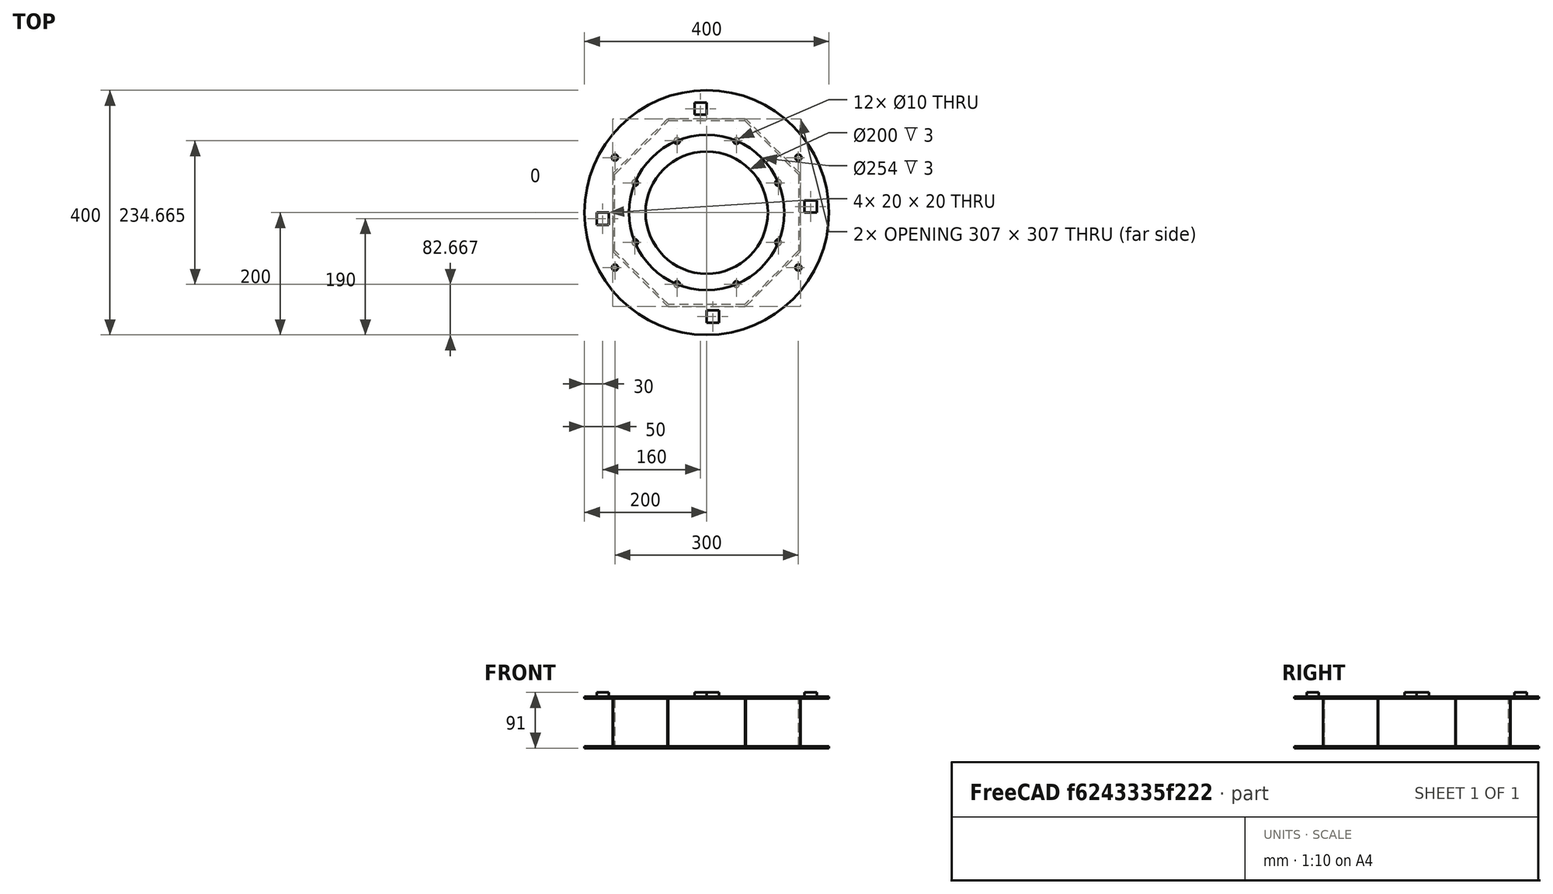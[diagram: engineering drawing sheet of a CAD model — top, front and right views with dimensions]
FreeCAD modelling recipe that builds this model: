
FCSTD DOCUMENT  (FreeCAD 0.21R33771 (Git))
Label: FEA_Model_MMv2
License: Creative Commons Attribution-ShareAlike 4.0
LicenseURL: https://creativecommons.org/licenses/by-sa/4.0/
objects: Fem::FemPostPipeline×13, Fem::FemMeshObjectPython×11, Fem::FemResultObjectPython×10, Sketcher::SketchObject×4, PartDesign::Pad×4, Fem::FemSolverObjectPython×4, Fem::ConstraintForce×4, PartDesign::Plane×1, PartDesign::PolarPattern×1, PartDesign::MultiTransform×1, App::MaterialObjectPython×1, PartDesign::Body×1, Fem::FemPostWarpVectorFilter×1, Fem::ConstraintFixed×1, App::TextDocument×1, Fem::FemAnalysis×1
note: 16 computed .brp shape members not serialized (recipe doc carries the construction recipe); baked Part::Feature solids carry a one-line shape summary decoded from their .brp

FEATURE [Sketcher::SketchObject] Sketch
  FullyConstrained = true
  MapMode = 5
  Support = -> [XY_Plane]
  sketch-geometry (22):
    g0: Circle CenterX=0 CenterY=0 CenterZ=0 NormalX=0 NormalY=0 NormalZ=1 AngleXU=0 Radius=100
    g1: Circle CenterX=0 CenterY=0 CenterZ=0 NormalX=0 NormalY=0 NormalZ=1 AngleXU=0 Radius=200
    g2: LineSegment StartX=-117.333 StartY=48.6008 StartZ=0 EndX=-117.333 EndY=-48.6008 EndZ=0
    g3: LineSegment StartX=-117.333 StartY=-48.6008 StartZ=0 EndX=-48.6008 EndY=-117.333 EndZ=0
    g4: LineSegment StartX=-48.6008 StartY=-117.333 StartZ=0 EndX=48.6008 EndY=-117.333 EndZ=0
    g5: LineSegment StartX=48.6008 StartY=-117.333 StartZ=0 EndX=117.333 EndY=-48.6008 EndZ=0
    g6: LineSegment StartX=117.333 StartY=-48.6008 StartZ=0 EndX=117.333 EndY=48.6008 EndZ=0
    g7: LineSegment StartX=117.333 StartY=48.6008 StartZ=0 EndX=48.6008 EndY=117.333 EndZ=0
    g8: LineSegment StartX=48.6008 StartY=117.333 StartZ=0 EndX=-48.6008 EndY=117.333 EndZ=0
    g9: LineSegment StartX=-48.6008 StartY=117.333 StartZ=0 EndX=-117.333 EndY=48.6008 EndZ=0
    g10: Circle CenterX=0 CenterY=0 CenterZ=0 NormalX=0 NormalY=0 NormalZ=1 AngleXU=0 Radius=127
    g11: Circle CenterX=-117.333 CenterY=48.6008 CenterZ=0 NormalX=0 NormalY=0 NormalZ=1 AngleXU=0 Radius=5
    g12: Circle CenterX=-48.6008 CenterY=117.333 CenterZ=0 NormalX=0 NormalY=0 NormalZ=1 AngleXU=0 Radius=5
    g13: Circle CenterX=48.6008 CenterY=117.333 CenterZ=0 NormalX=0 NormalY=0 NormalZ=1 AngleXU=0 Radius=5
    g14: Circle CenterX=117.333 CenterY=48.6008 CenterZ=0 NormalX=0 NormalY=0 NormalZ=1 AngleXU=0 Radius=5
    g15: Circle CenterX=117.333 CenterY=-48.6008 CenterZ=0 NormalX=0 NormalY=0 NormalZ=1 AngleXU=0 Radius=5
    g16: Circle CenterX=48.6008 CenterY=-117.333 CenterZ=0 NormalX=0 NormalY=0 NormalZ=1 AngleXU=0 Radius=5
    g17: Circle CenterX=-48.6008 CenterY=-117.333 CenterZ=0 NormalX=0 NormalY=0 NormalZ=1 AngleXU=0 Radius=5
    g18: Circle CenterX=-117.333 CenterY=-48.6008 CenterZ=0 NormalX=0 NormalY=0 NormalZ=1 AngleXU=0 Radius=5
    g19: LineSegment StartX=0 StartY=0 StartZ=0 EndX=-152 EndY=62.9605 EndZ=0
    g20: LineSegment StartX=0 StartY=0 StartZ=0 EndX=-152 EndY=-62.9605 EndZ=0
    g21: LineSegment StartX=-152 StartY=62.9605 StartZ=0 EndX=-152 EndY=-62.9605 EndZ=0
  constraints (49):
    c: Coincident(g0,g-1)
    c: Coincident(g1,g0)
    c: Diameter(g1) = 400
    c: Diameter(g0) = 200
    c: Coincident(g2,g3)
    c: Coincident(g3,g4)
    c: Coincident(g4,g5)
    c: Coincident(g5,g6)
    c: Coincident(g6,g7)
    c: Coincident(g7,g8)
    c: Coincident(g8,g9)
    c: Coincident(g9,g2)
    c: Equal(g2, g3-g9) x7
    c: PointOnObject(g2,g10)
    c: PointOnObject(g3,g10)
    c: PointOnObject(g4,g10)
    c: PointOnObject(g5,g10)
    c: PointOnObject(g6,g10)
    c: PointOnObject(g7,g10)
    c: PointOnObject(g8,g10)
    c: PointOnObject(g9,g10)
    c: Coincident(g10,g0)
    c: Vertical(g2)
    c: Diameter(g10) = 254
    c: Coincident(g11,g2)
    c: Diameter(g11) = 10
    c: Equal(g11,g12) = 10
    c: Coincident(g12,g8)
    c: Coincident(g13,g7)
    c: Equal(g13,g11)
    c: Coincident(g14,g6)
    c: Coincident(g15,g5)
    c: Coincident(g16,g4)
    c: Coincident(g17,g3)
    c: Coincident(g18,g2)
    c: Equal(g14,g15)
    c: Equal(g15,g16)
    c: Equal(g16,g17)
    c: Equal(g17,g18)
    c: Equal(g18,g11)
    c: Coincident(g19,g0)
    c: Coincident(g20,g0)
    c: PointOnObject(g18,g20)
    c: PointOnObject(g11,g19)
    c: Coincident(g21,g19)
    c: Coincident(g21,g20)
    c: Vertical(g21)
    c: DistanceX(g20,g0) = 152
    c: Distance(g21) = 125.921
FEATURE [PartDesign::Pad] Pad
  Direction = (0,0,1)
  Length = 3
  Length2 = 10
  Profile = -> Sketch
  ReferenceAxis = -> Sketch [N_Axis]
  Type = 0
FEATURE [Sketcher::SketchObject] Sketch001
  FullyConstrained = true
  MapMode = 5
  Support = -> [XY_Plane]
  sketch-geometry (7):
    g0: LineSegment StartX=-153.5 StartY=63 StartZ=0 EndX=-150.5 EndY=63 EndZ=0
    g1: LineSegment StartX=-150.5 StartY=63 StartZ=0 EndX=-150.5 EndY=-63 EndZ=0
    g2: LineSegment StartX=-150.5 StartY=-63 StartZ=0 EndX=-153.5 EndY=-63 EndZ=0
    g3: LineSegment StartX=-153.5 StartY=-63 StartZ=0 EndX=-153.5 EndY=63 EndZ=0
    g4: LineSegment StartX=-153.5 StartY=63 StartZ=0 EndX=-150.5 EndY=-63 EndZ=0
    g5: LineSegment StartX=-153.5 StartY=-63 StartZ=0 EndX=-150.5 EndY=63 EndZ=0
    g6: GeomPoint X=-152 Y=0 Z=0
  constraints (18):
    c: Coincident(g0,g1)
    c: Coincident(g1,g2)
    c: Coincident(g2,g3)
    c: Coincident(g3,g0)
    c: Horizontal(g0)
    c: Horizontal(g2)
    c: Vertical(g1)
    c: Vertical(g3)
    c: DistanceY(g3,g3) = 126
    c: DistanceX(g0,g0) = 3
    c: Coincident(g4,g0)
    c: Coincident(g4,g1)
    c: Coincident(g5,g2)
    c: Coincident(g5,g0)
    c: PointOnObject(g6,g4)
    c: PointOnObject(g6,g5)
    c: DistanceX(g6,g-1) = 152
    c: PointOnObject(g6,g-1)
FEATURE [PartDesign::Pad] Pad001
  BaseFeature = -> Pad
  Direction = (0,0,1)
  Length = 84
  Length2 = 10
  Profile = -> Sketch001
  ReferenceAxis = -> Sketch001 [N_Axis]
  Type = 0
FEATURE [PartDesign::Plane] DatumPlane
  AttachmentOffset = pos=(0,0,81) rot=(0,0,1;0rad)
  Length = 432
  MapMode = 5
  Placement = pos=(0,0,81) rot=(0,0,1;0rad)
  ResizeMode = 0
  Support = -> [XY_Plane]
  Width = 432
FEATURE [Sketcher::SketchObject] Sketch002
  FullyConstrained = true
  MapMode = 5
  Placement = pos=(0,0,81) rot=(0,0,1;0rad)
  Support = -> [DatumPlane]
  sketch-geometry (11):
    g0: Circle CenterX=0 CenterY=0 CenterZ=0 NormalX=0 NormalY=0 NormalZ=1 AngleXU=0 Radius=200
    g1: Circle CenterX=0 CenterY=0 CenterZ=0 NormalX=0 NormalY=0 NormalZ=1 AngleXU=0 Radius=127
    g2: Circle CenterX=-150 CenterY=90 CenterZ=0 NormalX=0 NormalY=0 NormalZ=1 AngleXU=0 Radius=5
    g3: Circle CenterX=-150 CenterY=-90 CenterZ=0 NormalX=0 NormalY=0 NormalZ=1 AngleXU=0 Radius=5
    g4: Circle CenterX=150 CenterY=90 CenterZ=0 NormalX=0 NormalY=0 NormalZ=1 AngleXU=0 Radius=5
    g5: Circle CenterX=150 CenterY=-90 CenterZ=0 NormalX=0 NormalY=0 NormalZ=1 AngleXU=0 Radius=5
    g6: LineSegment StartX=150 StartY=-90 StartZ=0 EndX=150 EndY=90 EndZ=0
    g7: LineSegment StartX=150 StartY=90 StartZ=0 EndX=-150 EndY=90 EndZ=0
    g8: LineSegment StartX=-150 StartY=90 StartZ=0 EndX=-150 EndY=-90 EndZ=0
    g9: LineSegment StartX=-150 StartY=-90 StartZ=0 EndX=150 EndY=-90 EndZ=0
    g10: GeomPoint X=0 Y=0 Z=0
  constraints (24):
    c: Diameter(g0) = 400
    c: Coincident(g1,g-1)
    c: Diameter(g1) = 254
    c: Coincident(g0,g1)
    c: Coincident(g6,g7)
    c: Coincident(g7,g8)
    c: Coincident(g8,g9)
    c: Coincident(g9,g6)
    c: Horizontal(g7)
    c: Horizontal(g9)
    c: Vertical(g6)
    c: Vertical(g8)
    c: Symmetric(g7,g6,g10)
    c: Coincident(g10,g0)
    c: Coincident(g7,g2)
    c: Coincident(g4,g6)
    c: Coincident(g5,g6)
    c: Coincident(g3,g8)
    c: Equal(g2,g4)
    c: Equal(g4,g5)
    c: Equal(g5,g3)
    c: Diameter(g2) = 10
    c: DistanceY(g8,g8) = 180
    c: DistanceX(g7,g7) = 300
FEATURE [PartDesign::Pad] Pad002
  BaseFeature = -> Pad001
  Direction = (0,0,1)
  Length = 3
  Length2 = 10
  Profile = -> Sketch002
  ReferenceAxis = -> Sketch002 [N_Axis]
  Type = 0
FEATURE [PartDesign::PolarPattern] PolarPattern
  Angle = 360
  Axis = -> Sketch001 [N_Axis]
  Occurrences = 8
FEATURE [PartDesign::MultiTransform] MultiTransform
  BaseFeature = -> Pad002
  Originals = -> [Pad001]
  Transformations = -> [PolarPattern]
FEATURE [App::MaterialObjectPython] MaterialSolid  # material (typed FeaturePython)
  Category = 0
  Material = AuthorAndLicense=(c) 2013 Juergen Riegel (CC-BY 3.0),CardName=Steel-Generic,Density=7900 kg/m^3,+9 more (map truncated)
FEATURE [Sketcher::SketchObject] Sketch003
  FullyConstrained = true
  MapMode = 5
  Placement = pos=(0,0,81) rot=(0,0,1;0rad)
  Support = -> [DatumPlane]
  sketch-geometry (20):
    g0: LineSegment StartX=160 StartY=20 StartZ=0 EndX=160 EndY=0 EndZ=0
    g1: LineSegment StartX=160 StartY=0 StartZ=0 EndX=180 EndY=0 EndZ=0
    g2: LineSegment StartX=180 StartY=0 StartZ=0 EndX=180 EndY=20 EndZ=0
    g3: LineSegment StartX=180 StartY=20 StartZ=0 EndX=160 EndY=20 EndZ=0
    g4: GeomPoint X=170 Y=10 Z=0
    g5: LineSegment StartX=-20 StartY=180 StartZ=0 EndX=-20 EndY=160 EndZ=0
    g6: LineSegment StartX=-20 StartY=160 StartZ=0 EndX=0 EndY=160 EndZ=0
    g7: LineSegment StartX=0 StartY=160 StartZ=0 EndX=0 EndY=180 EndZ=0
    g8: LineSegment StartX=0 StartY=180 StartZ=0 EndX=-20 EndY=180 EndZ=0
    g9: GeomPoint X=-10 Y=170 Z=0
    g10: LineSegment StartX=-180 StartY=0 StartZ=0 EndX=-180 EndY=-20 EndZ=0
    g11: LineSegment StartX=-180 StartY=-20 StartZ=0 EndX=-160 EndY=-20 EndZ=0
    g12: LineSegment StartX=-160 StartY=-20 StartZ=0 EndX=-160 EndY=0 EndZ=0
    g13: LineSegment StartX=-160 StartY=0 StartZ=0 EndX=-180 EndY=0 EndZ=0
    g14: GeomPoint X=-170 Y=-10 Z=0
    g15: LineSegment StartX=0 StartY=-160 StartZ=0 EndX=0 EndY=-180 EndZ=0
    g16: LineSegment StartX=0 StartY=-180 StartZ=0 EndX=20 EndY=-180 EndZ=0
    g17: LineSegment StartX=20 StartY=-180 StartZ=0 EndX=20 EndY=-160 EndZ=0
    g18: LineSegment StartX=20 StartY=-160 StartZ=0 EndX=0 EndY=-160 EndZ=0
    g19: GeomPoint X=10 Y=-170 Z=0
  constraints (52):
    c: Coincident(g0,g1)
    c: Coincident(g1,g2)
    c: Coincident(g2,g3)
    c: Coincident(g3,g0)
    c: Horizontal(g1)
    c: Horizontal(g3)
    c: Vertical(g0)
    c: Vertical(g2)
    c: Symmetric(g1,g0,g4)
    c: Coincident(g5,g6)
    c: Coincident(g6,g7)
    c: Coincident(g7,g8)
    c: Coincident(g8,g5)
    c: Horizontal(g6)
    c: Horizontal(g8)
    c: Vertical(g5)
    c: Vertical(g7)
    c: Symmetric(g6,g5,g9)
    c: Coincident(g10,g11)
    c: Coincident(g11,g12)
    c: Coincident(g12,g13)
    c: Coincident(g13,g10)
    c: Horizontal(g11)
    c: Horizontal(g13)
    c: Vertical(g10)
    c: Vertical(g12)
    c: Symmetric(g11,g10,g14)
    c: Coincident(g15,g16)
    c: Coincident(g16,g17)
    c: Coincident(g17,g18)
    c: Coincident(g18,g15)
    c: Horizontal(g16)
    c: Horizontal(g18)
    c: Vertical(g15)
    c: Vertical(g17)
    c: Symmetric(g16,g15,g19)
    c: DistanceX(g16,g16) = 20
    c: PointOnObject(g15,g-2)
    c: Equal(g17,g18)
    c: DistanceY(g19,g-1) = 170
    c: DistanceY(g-1,g9) = 170
    c: DistanceX(g-1,g4) = 170
    c: DistanceX(g14,g-1) = 170
    c: Equal(g18,g13)
    c: Equal(g13,g12)
    c: Equal(g12,g6)
    c: Equal(g6,g7)
    c: Equal(g7,g3)
    c: Equal(g3,g2)
    c: PointOnObject(g12,g-1)
    c: PointOnObject(g0,g-1)
    c: PointOnObject(g6,g-2)
FEATURE [PartDesign::Pad] Pad003
  BaseFeature = -> MultiTransform
  Direction = (0,0,1)
  Length = 10
  Length2 = 10
  Profile = -> Sketch003
  ReferenceAxis = -> Sketch003 [N_Axis]
  Type = 0
FEATURE [PartDesign::Body] Body
  Group = -> [Sketch,Pad,Sketch001,Pad001,DatumPlane,Sketch002,Pad002,MultiTransform,PolarPattern,Sketch003,Pad003]
  Origin = -> Origin
  Tip = -> Pad003
FEATURE [Fem::FemMeshObjectPython] FEMMeshGmsh  # FEM object (typed FeaturePython)
  Algorithm2D = 0
  Algorithm3D = 0
  CharacteristicLengthMax = 0
  CharacteristicLengthMin = 0
  CoherenceMesh = true
  ElementDimension = 0
  ElementOrder = 1
  GeometryTolerance = 1e-06
  GroupsOfNodes = false
  HighOrderOptimize = 0
  MeshSizeFromCurvature = 12
  OptimizeNetgen = false
  OptimizeStd = true
  Part = -> Pad003
  RecombinationAlgorithm = 0
  Recombine3DAll = false
  RecombineAll = false
  SecondOrderLinear = false
FEATURE [Fem::FemSolverObjectPython] SolverCalculix  # FEM object (typed FeaturePython)
  AnalysisType = 0
  BeamShellResultOutput3D = false
  BucklingFactors = 1
  EigenmodeHighLimit = 1000000
  EigenmodeLowLimit = 0
  EigenmodesCount = 10
  GeometricalNonlinearity = 0
  IterationsControlParameterCutb = 0.25,0.5,0.75,0.85,,,1.5,
  IterationsControlParameterIter = 4,8,9,200,10,400,,200,,
  IterationsControlParameterTimeUse = false
  IterationsThermoMechMaximum = 200
  IterationsUserDefinedIncrementations = false
  IterationsUserDefinedTimeStepLength = false
  MaterialNonlinearity = 0
  MatrixSolverType = 0
  SplitInputWriter = false
  ThermoMechSteadyState = true
  TimeEnd = 1
  TimeInitialStep = 1
FEATURE [Fem::FemPostWarpVectorFilter] WarpVector
  Factor = 49.51
  Vector = 0
FEATURE [Fem::FemPostPipeline] Pipeline_CalculiX_static_Results
  Filter = -> [WarpVector]
  Mode = 2
FEATURE [Fem::ConstraintFixed] ConstraintFixed
  NormalDirection = (1,-1e-16,0)
  Normals = (96) [(-1,0,0),(0.5,-0.866025,0),(0.5,0.866025,0),(-1,2.44929e-16,0),(-1,0,0),(0.5,-0.866025,0),(0.5,0.866025,0),(-1,2.44929e-16,0),(-1,0,0),+87 more]
  Points = (96) [(122.333,48.6008,3),(114.833,52.9309,3),(114.833,44.2707,3),(122.333,48.6008,3),(122.333,48.6008,1.5),(114.833,52.9309,1.5),(114.833,44.2707,1.5),+89 more]
  References = -> [Pad003]
  Scale = 2
FEATURE [Fem::FemSolverObjectPython] SolverCcxTools  # FEM object (typed FeaturePython)
  AnalysisType = 0
  BeamShellResultOutput3D = false
  BucklingFactors = 1
  EigenmodeHighLimit = 1000000
  EigenmodeLowLimit = 0
  EigenmodesCount = 10
  GeometricalNonlinearity = 0
  IterationsControlParameterCutb = 0.25,0.5,0.75,0.85,,,1.5,
  IterationsControlParameterIter = 4,8,9,200,10,400,,200,,
  IterationsControlParameterTimeUse = false
  IterationsThermoMechMaximum = 2000
  IterationsUserDefinedIncrementations = false
  IterationsUserDefinedTimeStepLength = false
  MaterialNonlinearity = 0
  MatrixSolverType = 0
  SplitInputWriter = false
  ThermoMechSteadyState = true
  TimeEnd = 1
  TimeInitialStep = 0.01
FEATURE [Fem::FemSolverObjectPython] SolverCalculix001  # FEM object (typed FeaturePython)
  AnalysisType = 0
  BeamShellResultOutput3D = false
  BucklingFactors = 1
  EigenmodeHighLimit = 1000000
  EigenmodeLowLimit = 0
  EigenmodesCount = 10
  GeometricalNonlinearity = 0
  IterationsControlParameterCutb = 0.25,0.5,0.75,0.85,,,1.5,
  IterationsControlParameterIter = 4,8,9,200,10,400,,200,,
  IterationsControlParameterTimeUse = false
  IterationsThermoMechMaximum = 2000
  IterationsUserDefinedIncrementations = false
  IterationsUserDefinedTimeStepLength = false
  MaterialNonlinearity = 0
  MatrixSolverType = 0
  SplitInputWriter = false
  ThermoMechSteadyState = true
  TimeEnd = 1
  TimeInitialStep = 0.01
FEATURE [Fem::FemPostPipeline] ResultPipeline
  Mode = 2
FEATURE [Fem::ConstraintForce] ConstraintForce
  Direction = -> Pad003 [Edge226]
  DirectionVector = (-0.707107,-0.707107,0)
  Force = 2850
  NormalDirection = (1,-1e-16,0)
  Points = (12) [(-145,90,84),(-152.5,94.3301,84),(-152.5,85.6699,84),(-145,90,84),(-145,90,82.5),(-152.5,94.3301,82.5),(-152.5,85.6699,82.5),(-145,90,82.5),+4 more]
  References = -> [Pad003]
  Reversed = true
  Scale = 2
FEATURE [Fem::ConstraintForce] ConstraintForce001
  Direction = -> Pad003 [Edge221]
  DirectionVector = (0.707107,-0.707107,0)
  Force = 2850
  NormalDirection = (1,-1e-16,0)
  Points = (12) [(-145,-90,84),(-152.5,-85.6699,84),(-152.5,-94.3301,84),(-145,-90,84),(-145,-90,82.5),(-152.5,-85.6699,82.5),(-152.5,-94.3301,82.5),(-145,-90,82.5),+4 more]
  References = -> [Pad003]
  Reversed = true
  Scale = 2
FEATURE [Fem::ConstraintForce] ConstraintForce002
  Direction = -> Pad003 [Edge233]
  DirectionVector = (0.707107,0.707107,0)
  Force = 2850
  NormalDirection = (1,-1e-16,0)
  Points = (12) [(155,-90,84),(147.5,-85.6699,84),(147.5,-94.3301,84),(155,-90,84),(155,-90,82.5),(147.5,-85.6699,82.5),(147.5,-94.3301,82.5),(155,-90,82.5),+4 more]
  References = -> [Pad003]
  Reversed = true
  Scale = 2
FEATURE [Fem::ConstraintForce] ConstraintForce003
  Direction = -> Pad003 [Edge238]
  DirectionVector = (-0.707107,0.707107,0)
  Force = 2850
  NormalDirection = (1,-1e-16,0)
  Points = (12) [(155,90,84),(147.5,94.3301,84),(147.5,85.6699,84),(155,90,84),(155,90,82.5),(147.5,94.3301,82.5),(147.5,85.6699,82.5),(155,90,82.5),(155,90,81),+3 more]
  References = -> [Pad003]
  Reversed = true
  Scale = 2
FEATURE [Fem::FemPostPipeline] Pipeline_CCX_Results
  Mode = 2
FEATURE [Fem::FemSolverObjectPython] SolverCcxTools001  # FEM object (typed FeaturePython)
  AnalysisType = 1
  BeamShellResultOutput3D = false
  BucklingFactors = 1
  EigenmodeHighLimit = 1000000
  EigenmodeLowLimit = 0
  EigenmodesCount = 10
  GeometricalNonlinearity = 0
  IterationsControlParameterCutb = 0.25,0.5,0.75,0.85,,,1.5,
  IterationsControlParameterIter = 4,8,9,200,10,400,,200,,
  IterationsControlParameterTimeUse = false
  IterationsThermoMechMaximum = 2000
  IterationsUserDefinedIncrementations = false
  IterationsUserDefinedTimeStepLength = false
  MaterialNonlinearity = 0
  MatrixSolverType = 0
  SplitInputWriter = false
  ThermoMechSteadyState = true
  TimeEnd = 1
  TimeInitialStep = 0.01
FEATURE [Fem::FemMeshObjectPython] CCX_EigenMode_1_Results_Mesh  # FEM object (typed FeaturePython)
FEATURE [Fem::FemResultObjectPython] CCX_EigenMode_1_Results  # FEM object (typed FeaturePython)
  DisplacementLengths = [36.1324,36.1311,13.4571,13.7361,13.6739,4.01533,3.89053,3.90667,7.97087,7.87766,8.06621,15.2902,15.0291,15.3227,13.6079,13.3328,13.549,3.83643,3.71415,3.72739,8.23995,8.13457,8.33602,15.4914,15.2266,15.5244,15.2129,15.5047,13.7167,13.4461,+7481 more]
  DisplacementVectors = (7511) [(0.814323,-0.0233713,36.1232),(-0.774746,0.108394,36.1226),(0.320202,0.191799,-13.4519),(0.332165,0.16695,-13.7311),(0.314468,0.210985,-13.6687),+7506 more]
  Eigenmode = 1
  EigenmodeFrequency = 549.841
  MaxShear = [326.363,690.179,4679.96,3288.88,2311.06,1362.16,1753.77,1194.57,1872.7,3116.93,2100.8,2626.94,5219.58,3126.36,2409.95,4439.1,2324.23,1156.75,1750.62,952.569,1577.39,3197.6,2128.25,3112.74,5216.01,3027.04,2280.24,2168.54,1534.44,1913.46,+7481 more]
  Mesh = -> CCX_EigenMode_1_Results_Mesh
  NodeNumbers = [1,2,3,4,5,6,7,8,9,10,11,12,13,14,15,16,17,18,19,20,21,22,23,24,25,26,27,28,29,30,31,32,33,34,35,36,37,38,39,40,41,42,43,44,45,46,47,48,49,50,51,52,53,54,55,56,57,58,59,60,61,62,63,64,65,66,67,68,69,+7442 more]
  NodeStrainXX = [0.0030878,-0.00487252,0.00209691,-0.0122655,-0.00823237,-0.0119638,-0.0136395,-0.0104847,0.0173261,0.0243868,0.0175075,0.00773248,-0.00128344,0.0106833,0.0090118,-0.00441965,0.0066169,0.0102703,0.0132308,0.00793071,-0.0137522,-0.0231871,+7489 more]
  NodeStrainXY = [-0.000585053,0.00067077,0.016592,0.00996236,0.00571926,-0.002227,-0.000847989,-0.00309526,-0.00129625,0.00251555,-0.000375481,0.00544919,0.0195384,0.00900183,-0.00725403,-0.0146643,-0.00575795,0.00227368,0.00162362,0.00241784,0.000148741,+7490 more]
  NodeStrainXZ = [0.000193783,-0.00042132,-0.0178555,-0.008414,-0.00605253,-0.00106414,-0.00188003,0.000762779,0.000496358,-0.00224992,-0.00350269,-0.00629089,-0.0182096,-0.00762218,-0.00599903,-0.0165288,-0.00563916,-0.00102333,-0.00189694,-0.000604541,+7491 more]
  NodeStrainYY = [-0.000980699,0.00396435,-0.0253691,-0.0207622,-0.0162432,0.000701833,0.00486517,0.000169847,0.00460781,-0.0055812,0.000871521,0.0198937,0.0298551,0.0215282,0.0161401,0.0262023,0.0181836,-0.00113573,-0.00512041,-0.00171642,-0.00183003,+7490 more]
  NodeStrainYZ = [-2.39986e-05,-8.19574e-05,-0.00925257,-0.00326347,-0.00607264,-0.00253608,-0.00523669,-0.00268604,0.00519186,0.0104622,0.00522376,0.00689375,0.00909602,0.00238753,-0.00287893,-0.00732202,-0.0040539,-0.00195279,-0.00507506,-0.00199882,+7491 more]
  NodeStrainZZ = [-0.000971946,0.000702889,0.00487403,0.0115162,0.00603745,0.0038036,0.00183234,0.00177993,-0.00449477,-0.0046059,-0.00610149,-0.00689876,-0.00542221,-0.010757,-0.00774489,-0.00425167,-0.0061495,-0.00292936,-0.00241025,-0.00147499,0.00392417,+7490 more]
  NodeStressXX = [606.024,-773.305,-1800.26,-4369.08,-3393.99,-2701.16,-2899.39,-2597.82,4677.77,5390.25,4110.11,3581.24,2473.63,4119.11,3394.94,1342.86,3170.02,2296.02,2693.22,1766.95,-3460.89,-5240.14,-4557.5,-4296.56,-1749.95,-4167.2,-802.523,1526.83,+7483 more]
  NodeStressXY = [-90.0082,103.195,2552.62,1532.67,879.886,-342.616,-130.46,-476.194,-199.424,387.007,-57.7663,838.337,3005.91,1384.9,-1116,-2256.04,-885.839,349.797,249.788,371.975,22.8832,-677.901,57.8014,-958.526,-2637.96,-1372.38,866.414,721.99,-786.365,+7482 more]
  NodeStressXZ = [29.8128,-64.8184,-2747,-1294.46,-931.159,-163.713,-289.236,117.351,76.3628,-346.141,-538.876,-967.83,-2801.48,-1172.64,-922.928,-2542.89,-867.564,-157.435,-291.836,-93.0063,-7.67475,-813.789,-519.898,-1167.99,-3015.96,-1144.45,-1613.09,+7484 more]
  NodeStressYY = [-19.8979,586.213,-6025.79,-5676.28,-4626.43,-752.602,-52.5145,-958.666,2721.11,779.782,1550.72,5452.21,7264.17,5787.55,4491.6,6053.93,4949.51,541.255,-130.045,282.778,-1626.71,-995.832,-2078.75,-6845.04,-6900.68,-5570.65,534.5,1292.9,+7483 more]
  NodeStressYZ = [-3.6921,-12.6088,-1423.47,-502.072,-934.252,-390.166,-805.645,-413.237,798.748,1609.57,803.655,1060.58,1399.39,367.312,-442.912,-1126.46,-623.676,-300.429,-780.779,-307.51,757.739,1797.89,652.862,844.166,1648.34,641.242,804.545,1503.35,+7483 more]
  NodeStressZZ = [-18.5513,84.4503,-1373.01,-710.362,-1198.64,-275.408,-519.104,-710.962,1320.71,929.829,477.954,1330.28,1836.9,820.588,816.982,1368.7,1205.96,265.311,286.902,319.922,-741.446,-1013.25,-687.845,-1637.66,-1468.97,-935.596,1564.57,1816.98,+7483 more]
  PrincipalMax = [620.123,594.602,2130.15,-127.089,-511.759,-56.4209,554.355,-336.99,4697.89,5433.85,4200.36,5878.95,8712.8,6582.51,5189.87,6962.19,5331.57,2384.61,2771.41,1872.23,-306.522,972.447,-377.945,-977.057,2395.74,-356.74,2448.38,3419.55,2470.16,+7482 more]
  PrincipalMed = [-19.9438,88.5119,-4099.43,-3923.79,-3573.43,-892.014,-1072.18,-1204.32,3069.2,2466.03,1939.66,3859.72,4588.27,3814.96,3143.69,3719.32,3310.8,646.866,808.497,530.322,-2061.23,-2798.91,-2311.71,-4599.67,-4479.07,-3905.89,960.276,2134.69,+7483 more]
  PrincipalMin = [-32.6042,-785.755,-7229.77,-6704.84,-5133.87,-2780.73,-2953.18,-2726.14,952.496,-800.017,-1.24336,625.06,-1726.36,329.782,369.965,-1916.02,683.118,71.1097,-729.828,-32.9056,-3461.3,-5422.75,-4634.44,-7202.54,-8036.27,-6410.82,-2112.1,+7484 more]
  ResultType = Fem::ResultMechanical
  Stats = [-9.62646,1.03652,-1.13205,2.49833,-38.9795,36.1232,0,38.9895,27.954,33045,-12778.5,50037.6,-18513,21074.7,-47505.4,14265,15.964,17997.5,0,0,0,0,0,0,0,0]
  Time = 0
  vonMises = [646.49,1209.52,8252.72,5719.09,4072.64,2417.37,3040.28,2094.78,3252.77,5400.75,3642.21,4590.41,9106.66,5426.89,4189.98,7781.25,4037.1,2086.09,3039.58,1695.21,2737.86,5568.05,3691.36,5415.48,9185.41,5268.92,4028.15,3858.57,2902.38,3381.27,+7481 more]
FEATURE [Fem::FemPostPipeline] Pipeline_CCX_EigenMode_1_Results
  Mode = 2
FEATURE [Fem::FemMeshObjectPython] CCX_EigenMode_2_Results_Mesh  # FEM object (typed FeaturePython)
FEATURE [Fem::FemResultObjectPython] CCX_EigenMode_2_Results  # FEM object (typed FeaturePython)
  DisplacementLengths = [6.51329,6.53195,7.57162,7.6697,7.76441,14.9444,14.6794,14.9693,13.2006,12.9296,13.1417,3.42169,3.30478,3.31378,8.67632,8.57171,8.77191,16.0953,15.8198,16.1245,14.3585,14.0734,14.3023,4.46825,4.337,4.35947,4.34683,4.36829,7.66528,7.57036,+7481 more]
  DisplacementVectors = (7511) [(-0.145361,0.0400156,-6.51154),(0.136509,0.499282,-6.51141),(-0.226865,-0.0161551,7.5682),(-0.224441,-0.00624625,7.66641),+7507 more]
  Eigenmode = 2
  EigenmodeFrequency = 553.372
  MaxShear = [227.809,319.677,2914.15,1795.08,1736.84,3291.25,5033,3340.74,3034.05,4553.4,2774.01,1131.31,1613.4,940.06,1503.66,3238.15,1941.03,2852.4,5939.57,3453.49,3073.78,5221.36,2924.27,1428.75,1928.39,1013.46,731.084,643.198,816.301,1109.01,+7481 more]
  Mesh = -> CCX_EigenMode_2_Results_Mesh
  NodeNumbers = <same value as first occurrence — deduplicated (x10 in doc)>
  NodeStrainXX = [-0.000534267,0.000894591,-0.0066109,0.000805463,-0.000318963,0.0262376,0.0326515,0.0274878,0.0229899,0.0306744,0.0197774,-0.00260738,-0.00557065,-0.00232457,-0.00127563,0.00778698,0.000144829,-0.0228726,-0.039422,-0.0242605,-0.0193644,+7490 more]
  NodeStrainXY = [-0.00143591,0.00190992,-0.00399284,-0.000417426,0.000431396,-0.00460572,-0.0146663,-0.00630401,0.00727778,0.0134133,0.00592587,-0.00212825,-0.000706947,-0.00250653,-0.000464858,0.00378831,-0.000372905,0.00465663,0.0173549,0.0099805,+7491 more]
  NodeStrainXZ = [-3.67507e-05,6.98318e-05,0.0096713,0.00491153,0.0033766,0.00691321,0.00945537,0.00102502,-0.000843828,-0.00533224,-0.00643939,-0.00158065,-0.0042878,-0.00174243,0.00413457,0.0109881,0.00391304,0.00494938,0.0116654,0.00532293,-0.00110557,+7490 more]
  NodeStrainYY = [0.000169063,-0.00073537,0.0213514,0.0157925,0.0160369,0.0109473,-0.00186988,0.0153707,0.015871,-0.000131314,0.00818204,0.0102649,0.0125375,0.00770444,-0.0133629,-0.0237003,-0.0182434,-0.0113823,0.000208486,-0.0112176,-0.0128824,+7490 more]
  NodeStrainYZ = [-8.03664e-05,-2.47868e-05,0.00420982,0.000511641,0.00316228,0.00726881,0.0183393,0.00874973,0.00762613,0.0159519,0.00726083,0.001324,0.00132411,-6.20299e-05,0.0016518,0.0043259,0.00207717,0.00704545,0.0191931,0.00889422,0.00947498,+7490 more]
  NodeStrainZZ = [0.000172538,-0.000125575,-0.00315999,-0.00460381,-0.00359594,-0.0108756,-0.00608187,-0.0101733,-0.00921824,-0.00807287,-0.00873185,-0.00182904,-0.00134988,-0.000965963,0.00349641,0.00337778,0.00432204,0.00911909,0.0105228,0.0101282,+7491 more]
  NodeStressXX = [-104.426,141.512,319.146,1507.86,1349.62,7072.26,7873.29,8000.27,6957.21,7311.86,5261.23,271.38,-208.909,151.67,-1481.88,-248.411,-1567.32,-6419.15,-9375.37,-6657.37,-5571.97,-7540.15,-6157.78,-687.418,123.113,-331.081,-333.684,180.815,+7483 more]
  NodeStressXY = [-220.909,293.833,-614.283,-64.2194,66.3687,-708.572,-2256.35,-969.847,1119.66,2063.59,911.673,-327.423,-108.761,-385.62,-71.5165,582.817,-57.37,716.405,2669.99,1535.46,-1366.22,-2514.84,-820.474,333.802,-31.3953,358.098,190.452,35.5568,+7483 more]
  NodeStressXZ = [-5.65396,10.7434,1487.89,755.62,519.478,1063.57,1454.67,157.696,-129.82,-820.345,-990.675,-243.176,-659.661,-268.067,636.088,1690.47,602.007,761.443,1794.68,818.912,-170.087,-1574.23,-962.765,-372.894,-857.109,-352.314,-351.678,-471.263,+7483 more]
  NodeStressYY = [3.77885,-109.252,4621.03,3813.56,3865.9,4719.91,2562.3,6136.11,5862,2572.52,3477.34,2251.73,2576.96,1694.59,-3341.46,-5092.61,-4396.29,-4651.4,-3278.38,-4650.77,-4574.73,-2950.38,-4510.54,-3060.34,-3057.21,-1941.77,311.273,619.451,-611.868,+7482 more]
  NodeStressYZ = [-12.3641,-3.81336,647.665,78.7139,486.505,1118.28,2821.42,1346.11,1173.25,2454.13,1117.05,203.693,203.708,-9.54306,254.123,665.522,319.565,1083.92,2952.78,1368.34,1457.69,3202.11,1073.47,144.132,363.545,129.235,443.21,346.394,562.622,+7482 more]
  NodeStressZZ = [4.31342,-15.4371,850.055,675.661,845.468,1362.54,1914.3,2206.26,2002.11,1350.74,875.203,391.125,440.439,360.687,-747.72,-926.75,-924.675,-1497.35,-1691.56,-1366.79,-1088.87,-1715.47,-1271.61,-601.439,-474.395,-461.099,464.218,661.868,+7483 more]
  PrincipalMax = [177.339,335.73,4763.15,3816.5,3950.8,7367.48,8730.94,8439.38,7705.67,8085.94,5701.48,2334.36,2607.26,1787.57,-368.871,1256.62,-547.93,-996.354,1443.86,-582.153,-477.459,1788.61,-699.394,-264.095,746.867,-16.9815,858.061,1116.74,173.769,+7482 more]
  PrincipalMed = [4.60477,-15.2836,2092.24,1954.25,1633.06,5002.27,4954,6145.35,5478.06,4170.05,3758.83,508.136,820.768,511.925,-1825.99,-2304.71,-1910.36,-4870.39,-5353.88,-4603.64,-4133.08,-5340.51,-4692.61,-963.507,-1045.45,-673.075,187.853,515.048,+7483 more]
  PrincipalMin = [-278.278,-303.624,-1065.16,226.336,477.126,784.968,-1335.05,1757.91,1637.58,-1020.87,153.468,71.7413,-619.541,-92.549,-3376.19,-5219.68,-4429.99,-6701.15,-10435.3,-7489.14,-6625.03,-8654.1,-6547.93,-3121.6,-3109.91,-2043.89,-604.107,+7484 more]
  ResultType = Fem::ResultMechanical
  Stats = [-1.3213,2.42548,-1.10315,9.64811,-37.3284,32.8618,0,37.3336,23.4424,32704.5,-14956.6,49674.6,-19728.2,21005.9,-46845.2,14052.6,12.8616,17811,0,0,0,0,0,0,0,0]
  Time = 0
  vonMises = [398.401,554.583,5053.32,3109.9,3063.87,5775.35,8807.43,5880.23,5316.64,7912.45,4876.11,2079.06,2799.85,1662.45,2604.83,5617.94,3411.39,5045.03,10323.4,6008.53,5355.65,9242.69,5176.55,2579.91,3342.84,1791.36,1267.74,1114.82,1416.04,1936.63,+7481 more]
FEATURE [Fem::FemPostPipeline] Pipeline_CCX_EigenMode_2_Results
  Mode = 2
FEATURE [Fem::FemMeshObjectPython] CCX_EigenMode_3_Results_Mesh  # FEM object (typed FeaturePython)
FEATURE [Fem::FemResultObjectPython] CCX_EigenMode_3_Results  # FEM object (typed FeaturePython)
  DisplacementLengths = [31.217,31.2143,11.9905,12.1456,12.1455,12.5627,12.3983,12.5618,12.7306,12.5681,12.7295,12.4572,12.2998,12.458,11.7886,11.6397,11.7797,11.1627,11.0257,11.1591,11.0755,10.9433,11.0805,11.5341,11.3969,11.5456,11.3825,11.5252,12.1205,11.9748,+7481 more]
  DisplacementVectors = (7511) [(-0.820739,0.0210017,-31.2062),(0.682129,-0.0663603,-31.2068),(0.298103,0.117281,-11.9862),(0.312323,0.0939068,-12.1412),(0.297959,0.147324,-12.141),+7506 more]
  Eigenmode = 3
  EigenmodeFrequency = 678.834
  MaxShear = [559.908,707.553,5032.04,3527.18,2764.19,3602.81,5128.34,3524.53,3538.45,5431.6,3549.66,2815.91,5073.6,3141,2538.38,4670.67,2710.45,2643.19,5073.6,2994.75,2836.84,4948.99,3074.48,3035.93,4710.93,2874.65,2107.29,2019.13,1666.83,2084.83,+7481 more]
  Mesh = -> CCX_EigenMode_3_Results_Mesh
  NodeNumbers = <same value as first occurrence — deduplicated (x10 in doc)>
  NodeStrainXX = [-0.00495147,0.00619949,0.00133501,-0.0146304,-0.00899124,-0.0294196,-0.0356375,-0.0299511,-0.0297828,-0.0402481,-0.0275088,-0.00902748,-0.00085625,-0.0134503,-0.0115766,0.00311605,-0.00790325,-0.0220898,-0.0355537,-0.0220697,-0.0201675,+7490 more]
  NodeStrainXY = [0.00045164,-0.000504169,0.0133483,0.00759626,0.00290537,0.00134883,0.0105882,0.00328865,-0.00343453,-0.00963628,-0.00241831,-0.00288177,-0.0159106,-0.00719426,0.00549341,0.0114458,0.0032998,0.00112725,0.0108922,0.00636012,-0.00501542,+7490 more]
  NodeStrainXZ = [-0.00031725,0.000483117,-0.020195,-0.00959158,-0.00706447,-0.00720964,-0.0103211,-0.00111607,0.000822391,0.00663366,0.00783074,0.00685272,0.0191741,0.00791875,0.00676081,0.0184487,0.00660248,0.00444091,0.0106174,0.00463932,-0.000990647,+7490 more]
  NodeStrainYY = [0.00225466,-0.00290552,-0.0316119,-0.024889,-0.0225362,-0.0136803,-0.00109254,-0.0187924,-0.0201497,-0.00122831,-0.010587,-0.0227485,-0.031513,-0.0221097,-0.0182311,-0.0306203,-0.0232201,-0.0112604,-0.00244684,-0.011805,-0.0133652,+7490 more]
  NodeStrainYZ = [1.949e-05,7.50706e-05,-0.00982677,-0.0027878,-0.00651686,-0.00789271,-0.0199874,-0.00980749,-0.0100541,-0.0202088,-0.00934921,-0.00699464,-0.00927176,-0.00218334,0.0031326,0.00807084,0.00426345,0.00641762,0.0175563,0.00816141,0.00932488,+7490 more]
  NodeStrainZZ = [0.00121211,-0.00176969,0.00694538,0.0132365,0.00786807,0.0128828,0.00817594,0.0119563,0.0120174,0.0113637,0.01229,0.00818662,0.0068162,0.0117887,0.00890927,0.00608543,0.00788699,0.00917822,0.0107147,0.00991046,0.0101578,0.00846089,+7489 more]
  NodeStressXX = [-933.077,1129.65,-2486.71,-5283.47,-4113.19,-8012.67,-8777.4,-8852.55,-8956.79,-9666.57,-7209.71,-4110.7,-3080.16,-4812.13,-4192.37,-1992.01,-3897.01,-6187.52,-8618.16,-6160.46,-5799.8,-8030.61,-6836.88,-4645.79,-2338.86,-4617.05,-653.572,+7484 more]
  NodeStressXY = [69.4831,-77.5644,2053.59,1168.65,446.98,207.512,1628.95,505.946,-528.389,-1482.51,-372.047,-443.349,-2447.78,-1106.81,845.141,1760.89,507.662,173.422,1675.73,978.48,-771.603,-1620,-205.792,-601.48,-2029.94,-1136.24,887.043,723.473,-849.367,+7482 more]
  NodeStressXZ = [-48.8077,74.3257,-3106.92,-1475.63,-1086.84,-1109.17,-1587.86,-171.702,126.522,1020.56,1204.73,1054.26,2949.86,1218.27,1040.12,2838.27,1015.77,683.216,1633.44,713.742,-152.407,-1560.68,-933.79,-1158.41,-2900.26,-1104.07,-1480.65,-1335.32,+7483 more]
  NodeStressYY = [175.559,-271.124,-7555.46,-6861.71,-6197.03,-5591.24,-3462.79,-7135.83,-7474.77,-3663.52,-4606.37,-6221.63,-7796.57,-6144.33,-5216.13,-7182.23,-6253.45,-4521.45,-3524.8,-4581.27,-4753.28,-3380.11,-4814.86,-6988.41,-6831.08,-5456.67,756.447,+7484 more]
  NodeStressYZ = [2.99846,11.5493,-1511.81,-428.892,-1002.59,-1214.26,-3074.98,-1508.84,-1546.79,-3109.05,-1438.34,-1076.1,-1426.43,-335.899,481.939,1241.67,655.915,987.326,2700.97,1255.6,1434.6,3219.59,1099.82,781.869,1540.9,598.313,806.899,1448.08,+7483 more]
  NodeStressZZ = [15.166,-96.3814,-1623.58,-996.249,-1519.45,-1504.6,-2036.87,-2405.25,-2525.99,-1726.28,-1086.83,-1462.38,-1899.78,-929.207,-1040.69,-1535.19,-1467.74,-1377.05,-1499.94,-1240.43,-1134.36,-1731.04,-1310.21,-1656.18,-1432.59,-975.251,1442.4,+7484 more]
  PrincipalMax = [179.897,1138.32,1750.37,-445.604,-897.921,-990.901,931.84,-1951.29,-2071.87,838.214,-342.699,-842.817,1305.21,-505.874,-617.619,1591.59,-980.257,-997.109,926.766,-640.997,-603.624,1299.9,-841.739,-1110.65,1774.29,-503.107,2289.95,3225.8,+7483 more]
  PrincipalMed = [17.6696,-99.3831,-5102.4,-5195.86,-4505.46,-5921.08,-5884.07,-7441.98,-7736.92,-5869.6,-5118.19,-4477.25,-5239.74,-4591.91,-4137.19,-4551.26,-4236.79,-4805.43,-5349.23,-4710.67,-4806.51,-5843.58,-5129.51,-4997.23,-4729.25,-4293.45,1179.96,+7484 more]
  PrincipalMin = [-939.918,-276.789,-8313.72,-7499.96,-6426.29,-8196.53,-9324.83,-9000.36,-9148.77,-10025,-7442.02,-6474.64,-8841.98,-6787.88,-5694.38,-7749.75,-6401.15,-6283.48,-9220.43,-6630.5,-6277.31,-8598.07,-6990.7,-7182.5,-7647.57,-6252.41,-1924.64,+7484 more]
  ResultType = Fem::ResultMechanical
  Stats = [-4.46728,4.09892,-3.60486,3.41194,-33.0743,2.02427,0,33.0859,48.3503,29255,-13037,39005.9,-18855.7,15657.7,-44318.7,12262.4,27.8907,15858.6,0,0,0,0,0,0,0,0]
  Time = 0
  vonMises = [1048.16,1335.27,8903.9,6230.48,4861.42,6379.87,9041.43,6413.48,6487.24,9493.98,6269.21,4945.51,8910.05,5521.85,4504.76,8222.7,4726.29,4724.07,8869.61,5297.27,5099.91,8848.35,5461.63,5326.74,8354.17,5062.54,3783.74,3645.37,3186.02,3748.81,+7481 more]
FEATURE [Fem::FemPostPipeline] Pipeline_CCX_EigenMode_3_Results
  Mode = 2
FEATURE [Fem::FemMeshObjectPython] CCX_EigenMode_4_Results_Mesh  # FEM object (typed FeaturePython)
FEATURE [Fem::FemResultObjectPython] CCX_EigenMode_4_Results  # FEM object (typed FeaturePython)
  DisplacementLengths = [39.9083,39.9016,8.00915,8.34118,8.26119,6.8274,6.64613,6.92752,9.24508,8.89757,9.17156,6.0076,5.84582,6.11394,8.65598,8.31787,8.58128,6.41875,6.24735,6.52273,8.9902,8.64699,8.91924,6.01444,5.85213,6.11894,5.83249,6.09414,8.31327,7.9904,+7481 more]
  DisplacementVectors = (7511) [(1.5938,0.0721658,39.8764),(-1.35173,-0.041129,39.8787),(-0.507994,0.0300343,7.99297),(-0.542016,0.0450534,8.32343),(-0.530265,0.0187294,8.24413),+7506 more]
  Eigenmode = 4
  EigenmodeFrequency = 935.02
  MaxShear = [1557.04,1763.69,3031.99,3392.41,2049.49,2247.1,3005.98,3550.91,4063.82,3560.99,2720.35,1754.36,2780.67,2914.55,2900.21,2817.68,2051.6,1963.99,3370.72,3306.15,3984.44,3921.15,2748.31,1934.89,2595.49,2880.06,1094.74,1652.73,1806.12,1283.46,+7481 more]
  Mesh = -> CCX_EigenMode_4_Results_Mesh
  NodeNumbers = <same value as first occurrence — deduplicated (x10 in doc)>
  NodeStrainXX = [0.0153367,-0.0164563,0.0150497,0.0265301,0.0171589,-0.00658496,-0.0118237,-0.0106641,-0.017178,-0.0237006,-0.0128704,0.0148474,0.0166423,0.0237075,0.0238551,0.0139364,0.0170309,-0.00317079,-0.0126432,-0.00706971,-0.0122119,-0.0199158,+7489 more]
  NodeStrainXY = [0.000768716,-0.000767976,-0.00604766,-0.00315324,-0.00118759,0.00304444,0.00703759,0.00362312,-0.000299972,-0.00352728,-0.000111535,0.00372447,0.00857555,0.00498989,-0.00270163,-0.00473565,-0.00162331,0.00391247,0.00976337,0.0072887,+7491 more]
  NodeStrainXZ = [0.00122953,-0.000815211,0.0134964,0.00714804,0.00509502,-0.00309883,-0.0049616,-0.00154585,0.00137241,0.00538704,0.00476275,-0.00381566,-0.00944415,-0.00428313,-0.00502451,-0.0123831,-0.00508676,0.00164844,0.0059293,0.00219045,-0.00115582,+7490 more]
  NodeStrainYY = [-0.00409494,0.0025398,0.0149907,0.0115834,0.00742426,-0.0198079,-0.0177296,-0.030099,-0.0340177,-0.0189825,-0.0209492,0.00184874,0.0079291,0.00565355,0.00916674,0.0168187,0.0104572,-0.0179291,-0.0198894,-0.0256657,-0.0316315,-0.0207241,+7489 more]
  NodeStrainYZ = [2.88667e-05,1.82835e-05,0.00695011,0.00201847,0.00459806,-0.00369552,-0.0117417,-0.00647512,-0.00871773,-0.0149853,-0.00665584,0.00377092,0.00513235,0.000875079,-0.00212478,-0.00615981,-0.00297484,0.00378892,0.0107791,0.00700318,0.00911591,+7490 more]
  NodeStrainZZ = [-0.00472385,0.00638212,-0.00830029,-0.0144511,-0.00590723,0.00709704,0.00827901,0.0134675,0.0157911,0.013492,0.0108093,-0.00334875,-0.00680129,-0.011848,-0.0118131,-0.0085621,-0.0068744,0.00499834,0.0100037,0.0120795,0.016371,0.011803,+7489 more]
  NodeStressXX = [3111.56,-3401.1,4823.81,6811.83,4794.74,-3239.51,-4273.76,-4790.11,-6727.93,-7014.45,-4635.11,3824.31,4610.75,5668.05,6117.17,4704.78,4998.65,-2345.68,-4544.58,-3471.03,-5048.65,-6391.32,-4756.56,4471.41,4174.45,5655.41,-138.719,-2112.31,+7483 more]
  NodeStressXY = [118.264,-118.15,-930.41,-485.114,-182.706,468.376,1082.71,557.403,-46.1495,-542.659,-17.1593,572.995,1319.31,767.675,-415.636,-728.561,-249.74,601.919,1502.06,1121.34,-464.287,-891.237,-11.4701,691.79,1084.4,849.265,-490.181,-865.371,+7483 more]
  NodeStressXZ = [189.158,-125.417,2076.36,1099.7,783.849,-476.742,-763.323,-237.823,211.14,828.776,732.731,-587.024,-1452.95,-658.944,-773.001,-1905.1,-782.578,253.606,912.199,336.992,-177.818,-1218.95,-589.999,575.148,1489.52,643.433,591.639,468.89,+7483 more]
  NodeStressYY = [122.075,-478.616,4814.75,4512.34,3297.11,-5273.8,-5182.36,-7780.1,-9318.66,-6288.6,-5877.99,1824.51,3270.26,2890.52,3857.43,5148.21,3987.3,-4616.18,-5659.39,-6331.95,-8036.27,-6515.67,-6429.08,2644.43,3019.95,2790.71,-413.454,-741.943,+7483 more]
  NodeStressYZ = [4.44103,2.81284,1069.25,310.534,707.394,-568.541,-1806.42,-996.172,-1341.19,-2305.44,-1023.98,580.141,789.592,134.628,-326.89,-947.663,-457.668,582.911,1658.32,1077.41,1402.45,2732.32,873.016,-388.933,-844.393,-261.411,-791.904,-1048.7,+7483 more]
  NodeStressZZ = [25.3197,112.509,1231.51,507.035,1246.11,-1134.59,-1181.03,-1077.55,-1655.76,-1292.52,-992.07,1024.89,1004.04,197.974,629.764,1243.48,1320.9,-1088.89,-1060.45,-524.992,-651.283,-1511.49,-1319.5,1130.73,871.322,310.996,-604.757,-428.345,+7483 more]
  PrincipalMax = [3127.77,117.063,5967.84,7069.86,4960.87,-931.873,-182.729,-906.725,-1419.02,-252.148,-655.166,4039.25,5593.49,5930.14,6280.15,5766.04,5179.03,-906.884,-106.048,-239.723,-379.515,30.6509,-1081.65,4754.61,5038.39,5942.75,865.997,773.761,+7483 more]
  PrincipalMed = [117.492,-473.952,4998.37,4476.31,3515.19,-3289.95,-4259.73,-4732.48,-6736.67,-6969.29,-4754.13,2103.94,3259.4,2725.38,3844.47,5199.76,4051.98,-2309,-4310.88,-3236.23,-5008.29,-6637.48,-4845.22,2607.11,3179.91,2631.72,-699.453,-1524.65,+7483 more]
  PrincipalMin = [13.6951,-3410.32,-96.1378,285.033,861.899,-5426.08,-6194.69,-8008.55,-9546.66,-7374.13,-6095.87,530.521,32.1537,101.03,479.742,130.669,1075.84,-4834.86,-6847.49,-6852.02,-8348.4,-7811.65,-6578.27,884.842,-152.582,182.644,-1323.47,-2531.71,+7483 more]
  ResultType = Fem::ResultMechanical
  Stats = [-19.5251,19.7549,-18.0926,18.161,-43.5429,41.0508,0,43.5622,62.6668,15473.6,-6760.51,21196.2,-9371.57,8298.72,-23192.7,6092.94,35.9156,8272.56,0,0,0,0,0,0,0,0]
  Time = 0
  vonMises = [3063.49,3272.15,5642.06,5929.89,3600.8,3893.68,5315.53,6156.5,7149.54,6928.44,4909.33,3044.03,4836.92,5056.49,5044.74,5374.65,3671.78,3447.82,5897.55,5734.78,6931.27,7326.13,4867.28,3358.06,4555.53,5006.99,1953.69,2934.53,3145.63,2321.17,+7481 more]
FEATURE [Fem::FemPostPipeline] Pipeline_CCX_EigenMode_4_Results
  Mode = 2
FEATURE [Fem::FemMeshObjectPython] CCX_EigenMode_5_Results_Mesh  # FEM object (typed FeaturePython)
FEATURE [Fem::FemResultObjectPython] CCX_EigenMode_5_Results  # FEM object (typed FeaturePython)
  DisplacementLengths = [7.17255,7.1547,6.57619,6.75447,6.8626,9.35218,8.9815,9.26607,6.339,6.17117,6.45148,8.99705,8.65047,8.92231,6.57106,6.40117,6.67899,9.35032,8.98415,9.26732,6.23773,6.05966,6.35066,8.79475,8.44929,8.7189,8.42791,8.69513,6.72978,6.55323,+7481 more]
  DisplacementVectors = (7511) [(0.289428,-0.575868,7.14353),(-0.253066,0.300023,7.14393),(0.212653,0.447285,-6.55751),(0.21381,0.456221,-6.73565),(0.220711,0.489206,-6.84158),+7506 more]
  Eigenmode = 5
  EigenmodeFrequency = 960.914
  MaxShear = [950.774,981.761,3186.87,2071.21,2786.76,4608.79,5032.48,4036.69,2968.95,4193.22,3551.76,3108.45,3590.87,2328.14,1722.94,3234.38,2797.69,3936,5222.4,3187.7,2149.41,3837.95,3520.86,3280.49,3563.94,2102.16,1358.63,1065.63,1075.53,1062.44,+7481 more]
  Mesh = -> CCX_EigenMode_5_Results_Mesh
  NodeNumbers = <same value as first occurrence — deduplicated (x10 in doc)>
  NodeStrainXX = [0.00286046,-0.00302115,0.00229233,-0.00171977,-0.00577422,-0.0300807,-0.0353798,-0.0279215,0.021299,0.0312992,0.0238523,0.0118773,0.00547162,0.0107052,-0.0014389,0.00260117,-0.00469806,-0.0261212,-0.0370686,-0.0227748,0.01603,0.0277541,+7489 more]
  NodeStrainXY = [-0.00589018,0.00611235,-0.00497504,-0.00667434,-0.00933299,-0.0132454,-0.00864712,-0.0118456,-0.012805,-0.0116712,-0.0125663,-0.00857154,-0.000969982,-0.00473182,-0.00712683,-0.00642017,-0.0101684,-0.0117629,-0.00751095,-0.00640119,+7491 more]
  NodeStrainXZ = [0.000230895,-0.000151738,-0.00978122,-0.00396006,-0.00373686,-0.00616349,-0.00909639,-0.000910268,-0.000449925,-0.00470259,-0.0055287,-0.00522334,-0.0134836,-0.00515925,0.00387044,0.00997694,0.0043846,0.00496503,0.0102971,0.0041021,+7491 more]
  NodeStrainYY = [-0.000815975,0.00053102,-0.0252496,-0.0174903,-0.0215984,-0.0209948,-0.0122376,-0.0207539,0.00754515,0.00282336,0.00862567,0.0223613,0.0278411,0.0175119,-0.0130158,-0.0247497,-0.0213468,-0.0174297,-0.0117248,-0.0148028,0.00209761,+7490 more]
  NodeStrainYZ = [-0.000304226,-0.000332043,-0.00371265,-5.8567e-05,-0.00301723,-0.00770158,-0.0177656,-0.00946649,0.00634754,0.0118696,0.00584699,0.00465305,0.00560013,0.00109346,0.00173028,0.00384074,0.00225637,0.00655456,0.0173778,0.00778505,-0.00371984,+7490 more]
  NodeStrainZZ = [-0.00086027,0.00116075,0.00646663,0.00461846,0.00885655,0.0170359,0.013803,0.0122747,-0.00592798,-0.0104144,-0.012223,-0.0107311,-0.00910904,-0.00863714,0.00281256,0.00648976,0.00840621,0.0141308,0.0157604,0.011387,-0.00402033,-0.00901141,+7489 more]
  NodeStressXX = [576.711,-618.181,-1550.1,-1948.23,-3024.81,-8555.45,-9344.71,-8495.71,5920.94,7550.82,6006.71,4539.68,3634.52,3906.16,-1564.7,-1406.6,-2758.01,-7413.28,-9514.37,-6525.82,4093.91,6777.12,6301.64,4527.41,2861.54,3412.64,298.437,-1308.7,+7483 more]
  NodeStressXY = [-906.181,940.362,-765.39,-1026.82,-1435.84,-2037.76,-1330.33,-1822.4,-1970,-1795.57,-1933.28,-1318.7,-149.228,-727.973,-1096.43,-987.719,-1564.37,-1809.68,-1155.53,-984.798,-1501.51,-1498.5,-1926.11,-1413.93,-445.006,-780.84,-488.475,+7484 more]
  NodeStressXZ = [35.5223,-23.3443,-1504.8,-609.24,-574.901,-948.229,-1399.44,-140.041,-69.2192,-723.475,-850.569,-803.59,-2074.39,-793.731,595.453,1534.91,674.554,763.851,1584.17,631.092,74.5737,1060.31,776.604,1031.3,2017.81,817.039,1111.37,835.194,+7483 more]
  NodeStressYY = [11.1058,-71.6939,-5787.32,-4374.47,-5459.3,-7157.62,-5784.37,-7393,3804.97,3169.92,3664.14,6152.6,7075.98,4953.35,-3345.76,-5614.42,-5319.35,-6076.12,-5615.33,-5299.36,1950.47,2966.79,4129.68,6629.85,6549.07,4380.19,-839.908,-1545.37,+7483 more]
  NodeStressYZ = [-46.8041,-51.0835,-571.177,-9.01031,-464.19,-1184.86,-2733.16,-1456.38,976.544,1826.09,899.537,715.854,861.558,168.225,266.198,590.883,347.134,1008.39,2673.51,1197.7,-572.283,-1792.92,-659.464,-530.543,-920.867,-379.099,-313.403,-499.063,+7483 more]
  NodeStressZZ = [4.29124,25.1878,-907.902,-973.12,-773.923,-1306.73,-1778.13,-2311.67,1732.18,1133.35,456.654,1061.46,1391.34,930.426,-910.625,-808.353,-741.968,-1220.66,-1386.84,-1270.16,1009.25,1120.89,690.207,1220.83,1113.03,1006.62,-941.157,-1128.44,+7483 more]
  PrincipalMax = [1245.75,639.222,309.917,-621.164,-632.202,-1032.68,-343.531,-1905.42,7158.55,8434.96,7301.02,7065.38,7272.82,5388.18,-504.566,461.536,-533.072,-992.265,1.0662,-918.411,4895.11,7700.57,7573.19,7483.67,6874.43,4954.48,1122.54,-370.246,+7483 more]
  PrincipalMed = [2.15492,20.3914,-2491.42,-1911.07,-2420.1,-5736.87,-6155.19,-6316.15,3078.89,3370.61,2628.98,3839.88,4737.95,3669.86,-1366.07,-2283.68,-2157.81,-4853.54,-6073.87,-4883.11,1562.22,3139.55,3016.85,3971.72,3902.65,3094.79,-1010.46,-1110.77,+7483 more]
  PrincipalMin = [-655.798,-1324.3,-6063.82,-4763.59,-6205.73,-10250.3,-10408.5,-9978.81,1220.65,48.52,197.506,848.476,91.0715,731.904,-3950.45,-6007.23,-6128.45,-8864.26,-10443.7,-7293.82,596.301,24.6738,531.481,922.695,-253.442,750.173,-1594.71,-2501.5,+7483 more]
  ResultType = Fem::ResultMechanical
  Stats = [-12.0264,11.9226,-11.8592,11.9006,-41.5505,42.2511,0,44.9947,49.6204,15645,-7236.26,23406.9,-9925.61,9586.18,-23906.4,6911.88,28.5032,8449.18,0,0,0,0,0,0,0,0]
  Time = 0
  vonMises = [1672.62,1738.76,5533.27,3671.54,4929.08,7983.23,8751.27,7001.75,5260.96,7314.93,6253,5385.27,6308.59,4078.3,3106.07,5623.43,4985.68,6817.76,9085.55,5575.67,3906.47,6686.73,6185.59,5686.68,6201.26,3649.11,2477.35,1874.13,1865.96,1912.39,+7481 more]
FEATURE [Fem::FemPostPipeline] Pipeline_CCX_EigenMode_5_Results
  Mode = 2
FEATURE [Fem::FemMeshObjectPython] CCX_EigenMode_6_Results_Mesh  # FEM object (typed FeaturePython)
FEATURE [Fem::FemResultObjectPython] CCX_EigenMode_6_Results  # FEM object (typed FeaturePython)
  DisplacementLengths = [6.68797,6.68627,3.14178,3.27845,3.2372,0.104079,0.107671,0.080179,0.31308,0.286811,0.305374,0.941799,0.907673,0.946854,0.304739,0.293045,0.294053,0.307025,0.270185,0.297393,2.27705,2.20982,2.33072,4.76755,4.59007,4.77916,4.58301,4.74287,+7483 more]
  DisplacementVectors = (7511) [(-0.313181,0.0537794,-6.68042),(0.264085,0.00693404,-6.68105),(0.210861,0.124236,-3.13223),(0.267713,0.108513,-3.2657),(0.245749,0.142884,-3.22469),+7506 more]
  Eigenmode = 6
  EigenmodeFrequency = 1142.52
  MaxShear = [360.398,372.342,5332.24,6133.87,3475.87,1694.17,1742.68,1358.45,338.413,272.981,302.927,551.998,730.112,743.265,590.944,523.382,357.879,289.374,561.414,561.027,3322.79,5926.41,5271.06,5666.55,6682.59,5971.7,2750.19,3531.11,3167.2,1815.5,+7481 more]
  Mesh = -> CCX_EigenMode_6_Results_Mesh
  NodeNumbers = <same value as first occurrence — deduplicated (x10 in doc)>
  NodeStrainXX = [-0.00340083,0.00346418,-0.0263841,-0.045636,-0.0269774,-0.0123216,-0.0108914,-0.00871271,-0.000671497,-0.000746364,-0.00155505,-0.0040505,-0.00396324,-0.00598689,-0.00493048,-0.0028174,-0.00284861,-0.000499323,-3.98838e-05,-0.000559212,+7491 more]
  NodeStrainXY = [0.000404048,-0.000382007,0.00813317,0.0104232,0.00259255,-0.00712035,-0.00684931,-0.00670123,0.000896797,0.00112041,0.00120072,0.000638489,-0.000446102,-0.000361967,0.00103251,0.000349692,0.000555959,0.00058623,0.00123317,0.00194956,+7491 more]
  NodeStrainXZ = [-0.000278012,0.000182101,-0.0255355,-0.0140228,-0.00979089,-0.00207106,-0.00332996,-0.000825721,3.27178e-05,0.000286777,0.000399647,0.0013898,0.00333431,0.00134779,0.000893143,0.00236525,0.000996262,7.20035e-05,0.00103847,0.000292071,+7491 more]
  NodeStrainYY = [0.00119608,-0.000508889,-0.0205066,-0.0174816,-0.01558,-0.000611415,0.00184726,0.00165915,0.00294651,0.00184542,0.00146375,-0.00292376,-0.00383381,-0.00253289,-0.000845675,-0.00186582,-0.00153759,-0.00226159,-0.00252453,-0.00373415,+7491 more]
  NodeStrainYZ = [2.49541e-05,2.32902e-05,-0.00955808,-0.0012232,-0.00465496,-0.00237261,-0.0046543,-0.00200282,3.16398e-05,-0.000145136,-0.000145695,-0.00104909,-0.00145875,-0.000265249,0.000515905,0.00136358,0.000670448,0.000975526,0.00279563,0.00159849,+7491 more]
  NodeStrainZZ = [0.000929269,-0.00132452,0.0150612,0.0255819,0.0126323,0.00506045,0.0029582,0.00132601,-0.00124043,-0.000449896,0.0001908,0.00194648,0.00234509,0.00324556,0.00218935,0.00144483,0.00101778,0.000751541,0.000741695,0.00166199,0.0104531,+7490 more]
  NodeStressXX = [-670.376,721.117,-7731.71,-11352,-7603.26,-2804,-2377.83,-2001.29,16.0675,-39.9218,-227.759,-1203.28,-1238.8,-1529.62,-1172.4,-807.105,-826.91,-308.67,-216.45,-389.652,-6125.79,-9267.87,-9481.58,-11245.6,-8875.27,-12080.8,243.122,6402.82,+7483 more]
  NodeStressXY = [62.1612,-58.7703,1251.26,1603.57,398.854,-1095.44,-1053.74,-1030.96,137.969,172.37,184.727,98.2291,-68.631,-55.6873,158.848,53.7987,85.5321,90.1892,189.718,299.932,1795.49,2393.1,2732.99,669.635,-489.359,-1268.58,-103.09,1231,-1520.28,+7482 more]
  NodeStressXZ = [-42.7711,28.0155,-3928.53,-2157.35,-1506.29,-318.625,-512.301,-127.034,5.0335,44.1195,61.4841,213.815,512.971,207.352,137.407,363.884,153.271,11.0775,159.765,44.934,-431.574,-1915.68,-1135.42,-2246.44,-5098.01,-2011.96,-2421.77,-2403.9,+7483 more]
  NodeStressYY = [36.8412,109.875,-6827.5,-7020.52,-5849.81,-1002.43,-418.031,-405.618,572.683,358.815,236.672,-1029.94,-1218.89,-998.239,-543.966,-660.709,-625.215,-579.788,-598.704,-878.104,-3941.93,-4648.62,-5883.79,-12399.5,-11285.2,-8837,-512.58,+7484 more]
  NodeStressYZ = [3.8391,3.58311,-1470.47,-188.185,-716.148,-365.017,-716.046,-308.126,4.86766,-22.3287,-22.4146,-161.398,-224.422,-40.8075,79.37,209.781,103.146,150.081,430.096,245.922,1021.24,3107.99,1177.29,1052.63,2076.82,715.305,1247.68,1106.34,+7483 more]
  NodeStressZZ = [-4.20678,-15.6064,-1355.52,-395.369,-1509.46,-129.838,-247.118,-456.869,-71.4604,5.68877,40.8342,-280.67,-268.288,-109.246,-77.0391,-151.377,-232.082,-116.229,-96.2071,-47.9295,-929.695,-1234.72,-951.785,-2356.32,-1723.18,-1298.85,-398.311,+7484 more]
  PrincipalMax = [42.2636,727.738,963.839,48.2048,-1028.44,6.02569,439.514,179.578,605.056,423.072,301.189,-210.342,-2.66212,-77.06,-40.1543,72.8271,-163.197,-66.1907,264.967,59.7589,-613.247,625.725,-650.34,-1749.48,1269.3,-826.363,2635.15,7677.81,7030.45,+7482 more]
  PrincipalMed = [-1.47232,104.595,-7177.92,-6596.56,-5953.92,-559.984,-436.654,-506.03,-15.9954,24.4013,53.2245,-989.21,-1260.43,-996.454,-531.209,-718.081,-642.055,-293.558,-318.468,-313.149,-3125.34,-4549.83,-4474.35,-11169.4,-11057.1,-8620.52,-437.686,+7484 more]
  PrincipalMin = [-678.533,-16.9466,-9700.65,-12219.5,-7980.18,-3382.31,-3045.84,-2537.32,-71.7704,-122.891,-304.666,-1314.34,-1462.89,-1563.59,-1222.04,-973.937,-878.955,-644.938,-857.86,-1062.3,-7258.83,-11227.1,-11192.5,-13082.6,-12095.9,-12769.8,+7485 more]
  ResultType = Fem::ResultMechanical
  Stats = [-20.3035,18.37,-5.70168,11.0182,-53.7494,106.014,0,106.146,17.8205,51067.9,-12622.7,43246.9,-49424.4,31078.5,-69996.1,6658.15,10.1014,29072.7,0,0,0,0,0,0,0,0]
  Time = 0
  vonMises = [699.954,691.966,9653.59,10636.5,6192.45,3143.78,3140.32,2447.22,650.734,489.238,527.556,982.637,1370.26,1299.37,1028.41,945.176,631.56,505.031,972.646,989.769,5812.06,10292.3,9243.72,10507.9,12877.2,10502.6,4774.38,6200.78,5565.29,3158.68,+7481 more]
FEATURE [Fem::FemPostPipeline] Pipeline_CCX_EigenMode_6_Results
  Mode = 2
FEATURE [Fem::FemMeshObjectPython] CCX_EigenMode_7_Results_Mesh  # FEM object (typed FeaturePython)
FEATURE [Fem::FemResultObjectPython] CCX_EigenMode_7_Results  # FEM object (typed FeaturePython)
  DisplacementLengths = [57.7184,57.7118,0.219055,0.25501,0.25093,0.754625,0.656536,0.731739,2.31489,2.24994,2.34962,4.56069,4.39276,4.57166,3.48026,3.33064,3.43374,0.633816,0.637,0.605936,0.0531877,0.0698163,0.0559054,0.568698,0.528117,0.54727,0.524135,0.545436,+7483 more]
  DisplacementVectors = (7511) [(-2.59166,-0.0980275,-57.6601),(2.30577,-0.191199,-57.6654),(-0.0150069,0.00100988,0.218538),(-0.0157122,0.0167211,0.253976),+7507 more]
  Eigenmode = 7
  EigenmodeFrequency = 1151.99
  MaxShear = [2554.07,3118.19,2146.84,1072.43,1129.26,1837.22,1913.36,1965,3272.33,4366.87,4160.6,5196.79,6524.35,6585.81,5534.63,5123.62,3735.5,1506.71,1811.67,1421.14,942.777,892.089,480.737,878.274,1480.26,775.639,554.991,758.368,743.568,527.69,+7481 more]
  Mesh = -> CCX_EigenMode_7_Results_Mesh
  NodeNumbers = <same value as first occurrence — deduplicated (x10 in doc)>
  NodeStrainXX = [-0.0237732,0.030652,-0.000992293,0.00130241,0.000233876,0.00983398,0.0136837,0.00942816,-0.0201308,-0.0302262,-0.0287749,-0.0294711,-0.0222441,-0.0470834,-0.039579,-0.0150225,-0.0243036,-0.00425324,0.00234019,0.00255759,0.00278694,+7490 more]
  NodeStrainXY = [0.000807531,-0.00148694,-0.0138541,-0.00678408,-0.00727036,0.00301233,0.00154708,0.00354165,0.00623066,0.00428967,0.00735569,0.00289887,-0.00616698,-0.0102411,0.0158095,0.0128832,0.00613846,-0.00826208,-0.0106589,-0.00856657,0.00533365,+7490 more]
  NodeStrainXZ = [-0.00411931,0.00251886,-0.000102807,0.000438264,-0.000517449,0.000745831,0.00179992,-0.0010457,0.00167052,0.00554848,0.00646614,0.0132401,0.03235,0.011325,0.00935525,0.0260856,0.0104395,-7.89389e-05,0.0018208,0.000991277,-0.00171703,+7490 more]
  NodeStrainYY = [0.00879817,-0.00932598,0.00227248,-0.00176723,0.0014983,0.0135033,0.00857342,0.0160757,-0.0236141,-0.0165006,-0.0166395,-0.0384739,-0.041584,-0.0297685,-0.0131878,-0.0219296,-0.0222801,0.00625615,0.00930442,0.00801713,0.00428732,0.00664694,+7489 more]
  NodeStrainYZ = [0.000369158,-2.72365e-05,-0.00033426,0.000179411,-0.000309186,0.00356976,0.00777431,0.00501229,-0.0084498,-0.0167033,-0.00813791,-0.00708886,-0.0132295,-0.00373968,0.00574868,0.0106937,0.00381189,-0.000188755,0.000599604,-0.00188405,+7491 more]
  NodeStrainZZ = [0.00660218,-0.00949993,0.000348454,0.000659683,-0.00233446,-0.00757384,-0.00639441,-0.00590541,0.010716,0.0153471,0.0178404,0.0224219,0.0205173,0.0308029,0.0211327,0.0114403,0.0149857,0.001283,-0.00347727,-0.00330725,-0.0017597,-0.00172631,+7489 more]
  NodeStressXX = [-4623.51,6080.25,35.2597,222.855,-33.5132,3331.77,3935.49,3711.85,-6908.07,-8270.9,-7608.51,-9786.68,-8419.58,-12557,-9739.15,-5254.83,-7384.93,-275.2,1302.41,1232.03,1041.98,615.689,743.887,86.6307,2280.27,764.032,-636.181,-1583.12,-282,+7482 more]
  NodeStressXY = [124.236,-228.761,-2131.41,-1043.7,-1118.52,463.436,238.013,544.869,958.563,659.949,1131.65,445.98,-948.766,-1575.56,2432.23,1982.04,944.378,-1271.09,-1639.83,-1317.93,820.561,649.13,437.052,544.357,496.378,631.276,-3.2689,-294.222,-129.377,+7482 more]
  NodeStressXZ = [-633.74,387.517,-15.8164,67.4252,-79.6075,114.743,276.91,-160.876,257.004,853.612,994.791,2036.93,4976.92,1742.3,1439.27,4013.17,1606.07,-12.1444,280.123,152.504,-264.159,-203.161,-96.3091,83.1816,749.697,34.3267,198.136,-359.381,50.1647,+7482 more]
  NodeStressYY = [387.466,-70.2136,537.533,-249.397,161.014,3896.28,3149.3,4734.55,-7443.97,-6159.27,-5741.53,-11171.7,-11395,-9893.12,-5678.97,-6317.45,-7073.62,1341.63,2373.83,2071.96,1272.81,1610.91,632.341,-341.457,181.84,-67.4416,-141.685,-477.91,+7483 more]
  NodeStressYZ = [56.7936,-4.19023,-51.4247,27.6016,-47.5671,549.194,1196.05,771.121,-1299.97,-2569.74,-1251.99,-1090.59,-2035.31,-575.336,884.412,1645.18,586.444,-29.0392,92.2467,-289.853,-364.65,-259.807,52.2387,-568.539,-379.349,-174.158,104.338,-127.605,+7483 more]
  NodeStressZZ = [49.6218,-96.9747,241.529,123.974,-428.641,653.649,846.554,1352.84,-2162.42,-1259.63,-436.925,-1803.14,-1840.91,-574.437,-398.887,-1183.62,-1340.42,576.53,407.42,329.746,342.496,322.718,305.181,518.975,450.872,363.087,380.307,-352.565,+7483 more]
  PrincipalMax = [396.865,6112.92,2432.91,1058.15,1186.71,4237.07,4157.15,5085.4,-1859.57,-124.73,-83.9473,-1221.11,1233.49,-259.963,107.921,2001.92,-836.796,2039.87,3565.81,3073.49,2100.52,1993.71,1130.46,850.56,2598.37,1107.95,435.578,-242.343,227.459,+7482 more]
  PrincipalMed = [127.99,-76.3962,242.179,125.975,-416.03,3082,3443.76,3558.44,-6250.66,-6706.59,-5297.88,-9925.73,-11073.8,-9333.01,-4963.6,-6512.49,-6654.37,576.658,575.389,329.043,341.806,346.083,381.957,319.575,676.76,395.054,-158.733,-412.172,-264.474,+7482 more]
  PrincipalMin = [-4711.28,-123.457,-1860.76,-1086.7,-1071.82,562.628,330.435,1155.4,-8404.23,-8858.48,-8405.14,-11614.7,-11815.2,-13431.6,-10961.3,-8245.33,-8307.8,-973.564,-57.5377,231.202,214.963,209.528,168.989,-905.987,-362.145,-443.328,-674.404,+7484 more]
  ResultType = Fem::ResultMechanical
  Stats = [-20.6072,20.0398,-9.72749,3.7352,-57.6654,111.459,0,111.547,75.7531,46458.3,-17753.8,54325.2,-52301.9,35433.6,-70569.2,11610.5,43.4223,26407.7,0,0,0,0,0,0,0,0]
  Time = 0
  vonMises = [4979.15,6212.98,3718.69,1862.78,2012.43,3254.46,3524.59,3431.56,5777.2,7881.3,7282.94,9660.47,12694.2,11675,9597.43,9500.1,6796.84,2610.07,3352,2794.65,1825.44,1719.97,874.658,1560.35,2601.59,1344.91,962.076,1439.36,1312.25,935.851,2135.08,+7480 more]
FEATURE [Fem::FemPostPipeline] Pipeline_CCX_EigenMode_7_Results
  Mode = 2
FEATURE [Fem::FemMeshObjectPython] CCX_EigenMode_8_Results_Mesh  # FEM object (typed FeaturePython)
FEATURE [Fem::FemResultObjectPython] CCX_EigenMode_8_Results  # FEM object (typed FeaturePython)
  DisplacementLengths = [6.53354,6.53043,2.1747,2.30202,2.3062,1.92926,1.82698,1.89867,0.0704753,0.0558524,0.0790583,0.465424,0.443856,0.472065,0.920632,0.873764,0.907305,1.53063,1.47481,1.55257,2.87873,2.70879,2.89795,0.379548,0.334348,0.32505,0.391477,0.392642,+7483 more]
  DisplacementVectors = (7511) [(-0.317315,-0.155073,-6.52399),(0.269132,-0.0846636,-6.52433),(0.196685,0.0123707,-2.16575),(0.234392,0.00348978,-2.29005),+7507 more]
  Eigenmode = 8
  EigenmodeFrequency = 1176.24
  MaxShear = [390.603,445.038,4095.64,4283.78,3138.32,3846.47,4101.93,3209.22,1676.15,2216.31,1910.05,1521.68,1654.03,998.086,610.18,603.326,645.383,1916.18,2930.25,2907.35,4808.86,7452.14,6280.92,4637.17,4444.08,4163.3,615.848,1921.33,2172.76,1510.45,+7481 more]
  Mesh = -> CCX_EigenMode_8_Results_Mesh
  NodeNumbers = <same value as first occurrence — deduplicated (x10 in doc)>
  NodeStrainXX = [-0.00357604,0.00412124,-0.0168676,-0.0310532,-0.0193844,-0.0251698,-0.0255673,-0.0207539,-0.0111014,-0.0149315,-0.0134229,-0.0024731,-0.00103327,-0.00508913,-0.005291,-0.0046777,-0.00390389,0.00790615,0.0123257,0.00831613,0.0287017,+7490 more]
  NodeStrainXY = [-0.000340519,6.38447e-05,0.00235354,0.0036849,-0.00240739,-0.0132288,-0.0116132,-0.0118798,0.005537,0.00599714,0.00532252,0.00316035,0.00216023,0.00175707,0.00172192,0.001964,0.00209107,0.000936267,-0.00135377,-0.00366902,-0.00955809,+7490 more]
  NodeStrainXZ = [-0.000495478,0.000189079,-0.0202568,-0.0104711,-0.00794806,-0.00477226,-0.00778913,-0.0020568,0.00172937,0.00418128,0.00348398,0.00276494,0.00614815,0.00206187,0.00019987,1.64678e-05,-1.46196e-05,-0.00159742,-0.0059281,-0.0020542,+7491 more]
  NodeStrainYY = [0.000326779,-0.000576205,-0.0253817,-0.0197403,-0.022342,-0.0137093,-0.00914578,-0.0132797,-0.00667633,-0.00309654,-0.00449162,-0.0125001,-0.0116954,-0.00700771,0.00119598,0.00193602,0.00327469,0.0159906,0.0178601,0.022468,0.0279299,+7490 more]
  NodeStrainYZ = [-5.3668e-05,8.95868e-07,-0.00775501,-0.00101701,-0.00411233,-0.00581613,-0.013349,-0.0066734,-0.00349248,-0.0067815,-0.00354385,-0.00266867,-0.00311544,-0.00133899,-0.000481877,-0.000559595,-0.000578722,-0.00421077,-0.0119932,-0.00692278,+7491 more]
  NodeStrainZZ = [0.00137346,-0.001651,0.0137601,0.0195807,0.0133827,0.0137816,0.0112224,0.00959651,0.00544088,0.00596681,0.00679144,0.00468649,0.00393974,0.00400143,0.00188203,0.000661229,-0.000160679,-0.00714784,-0.00995118,-0.011633,-0.0206582,-0.0220512,+7489 more]
  NodeStressXX = [-766.599,852.58,-5882.23,-8378.89,-6252.63,-6768.14,-6643.9,-6012.58,-3131.4,-3688.84,-3348.49,-1567.41,-1173.07,-1717.03,-1069.35,-959.697,-691.739,3148.9,4231.03,3489.14,8566.44,12083.3,11547.8,-1585.91,-3027.45,-4230.54,359.924,1832.16,+7483 more]
  NodeStressXY = [-52.3876,9.82226,362.083,566.908,-370.368,-2035.2,-1786.65,-1827.67,851.846,922.636,818.849,486.207,332.344,270.319,264.911,302.154,321.703,144.041,-208.272,-564.465,-1470.48,-2213.91,-2726.75,-3133.24,-2588.21,-2944.91,142.049,1200.41,+7483 more]
  NodeStressXZ = [-76.2274,29.0891,-3116.43,-1610.93,-1222.78,-734.194,-1198.33,-316.431,266.058,643.274,535.997,425.375,945.869,317.21,30.7492,2.53351,-2.24917,-245.756,-912.015,-316.03,568.614,2397.28,1276.13,363.488,93.2928,-195.2,-49.0179,160.198,+7483 more]
  NodeStressYY = [-166.165,129.896,-7192.08,-6638.44,-6707.65,-5005,-4117.51,-4862.69,-2450.61,-1868.08,-1974.45,-3110.02,-2813.4,-2012.19,-71.349,57.798,412.658,4392.67,5082.47,5666.35,8447.7,8470.44,9330.44,5116.78,4155.79,1445.15,-237.499,-804.126,+7483 more]
  NodeStressYZ = [-8.25662,0.137826,-1193.08,-156.462,-632.666,-894.79,-2053.7,-1026.68,-537.305,-1043.31,-545.208,-410.564,-479.299,-205.999,-74.135,-86.0915,-89.0341,-647.811,-1845.11,-1065.04,-1633.19,-4229.13,-1535.62,-703.122,-397.1,-600.424,-530.91,+7484 more]
  NodeStressZZ = [-5.13817,-35.4582,-1170.27,-589.058,-1211.55,-775.63,-983.951,-1343.28,-586.427,-473.714,-238.594,-465.93,-407.993,-318.481,34.1983,-138.324,-115.86,832.903,803.815,420.039,972.611,1755.89,1471.6,6.21599,139.831,911.133,-210.236,-598.015,+7483 more]
  PrincipalMax = [2.47406,853.665,575.248,-258.091,-881.346,-575.04,46.025,-1058.53,-442.066,89.2599,-52.6255,-299.851,245.126,-237.756,83.0981,163.284,511.479,4531.74,5778.99,5973.53,10240.5,14495,13684.5,6449.57,5025.03,2817.3,472.608,2297.1,5007.23,+7482 more]
  PrincipalMed = [-161.645,129.763,-7203.8,-6522.65,-6132.5,-3705.74,-3633.55,-3683.06,-1932,-1776.54,-1636.18,-1500.29,-1576.66,-1576.02,-52.3373,-160.139,-127.132,3143.35,4419.85,3443.16,7123.42,8224,7542.67,-87.7181,106.272,817.741,198.669,-321.521,+7483 more]
  PrincipalMin = [-778.731,-36.4102,-7616.03,-8825.64,-7157.99,-8267.99,-8157.83,-7476.97,-3794.37,-4343.35,-3872.73,-3343.22,-3062.93,-2233.93,-1137.26,-1043.37,-779.288,699.383,-81.5203,158.838,622.804,-409.323,1122.66,-2824.77,-3863.13,-5509.3,-759.088,+7484 more]
  ResultType = Fem::ResultMechanical
  Stats = [-14.1613,14.6316,-13.0135,3.13949,-118.171,84.0037,0,118.291,34.2831,39520.2,-10698.9,60790.8,-33985.4,35827,-46977.1,15226.4,19.7324,22782.2,0,0,0,0,0,0,0,0]
  Time = 0
  vonMises = [713.447,819.72,7993.14,7679.56,5831.91,6700.63,7117.29,5589.2,2909.15,3854.72,3324.38,2655.14,2869.76,1761.89,1158.59,1081.83,1117.86,3360.62,5312.96,5049.76,8499.26,12961.4,10879.8,8253.51,7712,7528.68,1120.14,3400.1,3778.52,2663.13,+7481 more]
FEATURE [Fem::FemPostPipeline] Pipeline_CCX_EigenMode_8_Results
  Mode = 2
FEATURE [Fem::FemMeshObjectPython] CCX_EigenMode_9_Results_Mesh  # FEM object (typed FeaturePython)
FEATURE [Fem::FemResultObjectPython] CCX_EigenMode_9_Results  # FEM object (typed FeaturePython)
  DisplacementLengths = [36.3983,36.4049,1.69869,1.8004,1.80364,0.0322507,0.036399,0.024997,3.19026,3.00261,3.23316,0.994357,0.905463,0.9192,2.89759,2.75042,2.9045,1.78527,1.6519,1.72263,1.7957,1.68979,1.82559,0.789203,0.725124,0.748671,0.718251,0.742598,1.78722,+7482 more]
  DisplacementVectors = (7511) [(1.54937,-0.0612541,36.3653),(-1.68787,-0.169811,36.3654),(-0.122031,-0.110557,1.69069),(-0.140723,-0.108066,1.79164),(-0.138282,-0.12664,1.79387),+7506 more]
  Eigenmode = 9
  EigenmodeFrequency = 1195.85
  MaxShear = [2306.5,1676.44,2048.61,1943.87,1737.94,1840.31,2009.14,2084.71,7025.95,9112.22,7858.3,5313.55,5689.37,4780.94,4663.73,6045.62,4935.06,5025.81,5831.74,3485.95,2395.77,3843.24,3446.28,2329.81,2009.79,2080.23,351.709,913.568,931.298,727.691,+7481 more]
  Mesh = -> CCX_EigenMode_9_Results_Mesh
  NodeNumbers = <same value as first occurrence — deduplicated (x10 in doc)>
  NodeStrainXX = [0.0199856,-0.0155287,0.00875458,0.0147015,0.0105365,0.0109414,0.0106134,0.00744209,-0.0450396,-0.0629111,-0.0522491,0.0134592,0.0256252,0.0261457,0.0346012,0.0210105,0.0260845,0.0365481,0.0389932,0.0269834,-0.0151137,-0.0249274,-0.0225656,+7488 more]
  NodeStrainXY = [0.00244711,-0.00282256,-0.000563172,-0.000254606,0.00239562,0.00884757,0.00900671,0.00939902,0.0259245,0.0261326,0.0249158,0.021963,0.022983,0.0223369,-0.00212495,0.00519607,0.00736001,0.0194519,0.0198346,0.0140839,0.00884856,0.0109961,+7489 more]
  NodeStrainXZ = [-0.00591999,-0.000102243,0.0093123,0.00414383,0.00366167,0.000852744,0.0012719,-0.00058201,0.00474664,0.0139783,0.0123187,0.00165925,0.00222562,-0.00273012,-0.0104421,-0.0244703,-0.0107585,-0.00618426,-0.0113406,-0.00498694,-0.00185702,+7490 more]
  NodeStrainYY = [-0.00810656,0.00551913,0.0134105,0.00993484,0.011782,-0.00489178,-0.00814579,-0.0120294,-0.0291996,-0.0174246,-0.0235111,-0.0393789,-0.0319568,-0.0160217,0.0234228,0.0363539,0.0358073,0.00828569,0.00387074,0.00253288,-0.00916702,+7490 more]
  NodeStrainYZ = [0.000101703,5.70484e-05,0.00385177,0.000628951,0.00211446,0.00117524,0.000142714,5.4619e-05,-0.0140133,-0.0255737,-0.0129882,-0.0043051,-0.00252,-0.00386064,-0.00339391,-0.0137876,-0.00561525,-0.00598352,-0.0156133,-0.00547932,0.00371068,+7490 more]
  NodeStrainZZ = [-0.00455056,0.00292995,-0.00708351,-0.00914352,-0.00738795,-0.0031682,-0.000785363,0.00298632,0.0217423,0.026575,0.028922,0.0109197,0.00136662,-0.00873904,-0.0218234,-0.0195112,-0.020032,-0.0163677,-0.0147184,-0.00855143,0.00847404,+7490 more]
  NodeStressXX = [3920.31,-3205.9,3087.04,4049.41,3343.76,2015.77,1826.94,960.204,-12986.5,-15881.8,-13442.7,339.889,3369.46,4182.21,9500.25,7600.06,8842.98,8907.34,9246.51,6570.32,-4149.03,-6355.82,-6034.31,-412.866,498.473,1463.81,-177.505,-102.88,+7483 more]
  NodeStressXY = [376.479,-434.24,-86.6418,-39.1701,368.557,1361.16,1385.65,1446,3988.38,4020.41,3833.2,3378.92,3535.84,3436.45,-326.916,799.396,1132.31,2992.6,3051.48,2166.75,1361.32,1691.71,1843.24,1627.81,973.178,1385.95,-131.052,-695.82,95.7605,-23.3974,+7481 more]
  NodeStressXZ = [-910.767,-15.7297,1432.66,637.512,563.334,131.191,195.676,-89.54,730.252,2150.51,1895.18,255.269,342.403,-420.019,-1606.48,-3764.65,-1655.15,-951.425,-1744.7,-767.221,-285.695,-1184.55,-708.88,-387.92,-388.649,-109.621,-180.039,-465.751,+7483 more]
  NodeStressYY = [-401.565,32.2204,3803.33,3316.07,3535.37,-420.106,-1059.09,-2035.42,-10549.6,-8883.85,-9021.52,-7789.06,-5489.32,-2305.08,7780.5,9960.58,10338.8,4559.27,3843.06,2808.7,-3234.16,-3698.81,-4439.66,-3502.82,-2797.85,-1551.88,-77.1631,490.045,+7483 more]
  NodeStressYZ = [15.6466,8.77668,592.581,96.7617,325.302,180.806,21.956,8.40292,-2155.89,-3934.42,-1998.18,-662.324,-387.692,-593.944,-522.14,-2121.17,-863.885,-920.542,-2402.04,-842.973,570.873,1761.63,656.267,312.515,546.937,350.592,223.973,52.0021,+7483 more]
  NodeStressZZ = [145.512,-366.114,650.408,380.941,586.15,-154.94,73.2819,274.702,-2712.36,-2114.68,-954.881,-50.8088,-362.634,-1184.67,819.549,1365.95,1748.13,766.434,983.186,1103.42,-520.148,-868.971,-630.942,-66.9026,-168.115,-60.0633,237.778,663.813,+7483 more]
  PrincipalMax = [4157.57,89.6958,4000.58,4157.64,3931,2637.77,2399.98,1549.31,-2149.43,-303.679,-402.273,1561.11,4615.34,5720.02,9814.42,11445.5,11210.4,10595.5,11281.1,7725.38,-404.92,-3.53252,-487.354,411.035,824.166,2004.31,433.65,1162.6,-265.783,+7482 more]
  PrincipalMed = [-37.8709,-366.296,3636.83,3318.88,3079.16,-154.204,59.4554,270.285,-7897.7,-8048.53,-6897.96,4.91058,-334.43,-1185.7,7798.93,8126.85,8379.25,3093.59,3173.94,2003.58,-2301.95,-3230.06,-3237.64,-145.033,-96.2371,3.69987,-180.772,552.92,+7483 more]
  PrincipalMin = [-455.438,-3263.19,-96.6323,269.9,455.116,-1042.84,-1618.3,-2620.11,-16201.3,-18528.1,-16118.9,-9066,-6763.4,-3841.86,486.956,-645.747,1340.27,543.914,-382.333,753.485,-5196.47,-7690.01,-7379.92,-4248.59,-3195.42,-2156.15,-269.768,-664.539,+7483 more]
  ResultType = Fem::ResultMechanical
  Stats = [-14.0583,12.4597,-13.4319,6.03847,-71.8603,114.704,0,114.898,49.5722,110486,-47151.1,148128,-48532,51919,-158321,36132,28.3639,55997.8,0,0,0,0,0,0,0,0]
  Time = 0
  vonMises = [4419.04,3149.75,3927.99,3543.61,3137.92,3326.54,3495.68,3699.62,12236.2,15842,13679,9940.79,9882,8549.09,8500.84,10820.6,8802.89,9050.28,10354,6438.52,4179.47,6685.19,6009.58,4407.98,3647.55,3603.94,663.412,1611.26,1613.56,1261.33,2186.42,+7480 more]
FEATURE [Fem::FemPostPipeline] Pipeline_CCX_EigenMode_9_Results
  Mode = 2
FEATURE [Fem::FemMeshObjectPython] CCX_EigenMode_10_Results_Mesh  # FEM object (typed FeaturePython)
FEATURE [Fem::FemResultObjectPython] CCX_EigenMode_10_Results  # FEM object (typed FeaturePython)
  DisplacementLengths = [27.5078,27.5083,0.375677,0.38955,0.433235,2.07405,1.89452,2.0434,0.738819,0.674661,0.733691,0.548525,0.508335,0.565452,0.764072,0.777068,0.813635,2.14561,1.94598,2.10094,0.410533,0.373661,0.382261,0.943118,0.870876,0.947705,0.871757,+7484 more]
  DisplacementVectors = (7511) [(-1.32859,-0.0513733,-27.4756),(1.30414,-0.00569383,-27.4774),(-0.069298,-0.0185979,0.368762),(-0.0444011,-0.0314051,0.385735),+7507 more]
  Eigenmode = 10
  EigenmodeFrequency = 1219.44
  MaxShear = [1544.18,1874.08,3331.71,3064.61,3291.59,6380.43,6959.45,5737.43,2726.59,3110.61,2402.76,1844.02,1884.68,2854.6,4169.67,4890.24,4859.27,7177.53,9099.64,5899.12,3122.81,2732.32,1607.04,1923.47,2184.99,2596.71,734.711,1276.74,1781.9,548.828,+7481 more]
  Mesh = -> CCX_EigenMode_10_Results_Mesh
  NodeNumbers = <same value as first occurrence — deduplicated (x10 in doc)>
  NodeStrainXX = [-0.0115692,0.0165561,-0.0147053,-0.0169209,-0.00786759,0.0400636,0.0432797,0.0346618,0.0146856,0.0191272,0.014374,-0.0131237,-0.0151176,-0.0228101,-0.0187307,-0.0149026,-0.00899426,0.0490312,0.0573414,0.0399639,0.00205479,0.000642949,+7489 more]
  NodeStrainXY = [0.000600921,-0.000543296,0.0105949,0.0125181,0.0126539,0.0201068,0.0175713,0.0184665,-0.00650551,-0.0075945,-0.00633115,-0.00647608,-0.0064255,-0.00907574,0.0198367,0.0213095,0.023065,0.0214248,0.0195586,0.0102372,0.00903832,0.00802984,+7489 more]
  NodeStrainXZ = [-0.00680015,0.00184896,0.00177628,-0.0016099,0.00113351,0.0074237,0.0124408,0.00339258,-0.00251647,-0.00611832,-0.00440229,0.00190846,0.00418851,0.000909046,-0.002141,-0.00577247,-0.0033704,-0.00832202,-0.0185428,-0.00738117,1.81449e-05,+7490 more]
  NodeStrainYY = [0.00504891,-0.0076181,0.0225651,0.0135668,0.0263022,0.0284259,0.0208306,0.0299162,0.0169865,0.00987521,0.0112574,0.00677409,0.00275935,0.000535848,0.0170095,0.0290051,0.032716,0.0282617,0.0261839,0.0297865,0.0244549,0.0187708,0.0149491,+7488 more]
  NodeStrainYZ = [0.000123036,-0.00016741,0.00288252,0.00227095,0.00297052,0.0098198,0.0227859,0.0118015,0.00561664,0.00980762,0.00485556,0.000507082,-0.00039861,0.000527929,-0.00368756,-0.00804632,-0.00623622,-0.0110659,-0.0298702,-0.0139195,-0.00615572,+7490 more]
  NodeStrainZZ = [0.00315066,-0.00494477,-0.00224186,0.0049496,-0.00738211,-0.0240161,-0.0209968,-0.0194813,-0.0108234,-0.00976756,-0.00902203,0.00167389,0.00448741,0.0111237,0.00420127,-0.00517986,-0.00876946,-0.0266165,-0.0285158,-0.0240224,-0.0108562,+7490 more]
  NodeStressXX = [-2168.67,3007.84,-1614.13,-2419.13,64.891,11295.2,11633,10536,4664.95,5162.06,4127.85,-2558.54,-3233.96,-4795.85,-2595.48,-1263.17,341.531,13390.5,15169,11424.6,2122.3,1616.51,980.531,-4101.8,-3410.52,-4500.24,88.8912,2368.14,1722,329.419,+7481 more]
  NodeStressXY = [92.4495,-83.5841,1629.98,1925.85,1946.76,3093.36,2703.28,2841.01,-1000.85,-1168.38,-974.023,-996.32,-988.538,-1396.27,3051.8,3278.38,3548.46,3296.12,3009.02,1574.95,1390.51,1235.36,820.883,-366.122,-769.439,-828.772,-136.071,391.86,+7483 more]
  NodeStressXZ = [-1046.18,284.456,273.273,-247.677,174.387,1142.11,1913.96,521.936,-387.15,-941.279,-677.275,293.608,644.386,139.853,-329.384,-888.072,-518.523,-1280.31,-2852.75,-1135.56,2.79152,299.111,-59.1764,-583.935,-1244.24,-631.132,-638.855,-778.701,+7483 more]
  NodeStressYY = [387.956,-711.262,4119.77,2271.3,5321.78,9504.76,8179.35,9805.95,5018.93,3738.67,3648.37,502.662,-483.66,-1204.17,2903,5491.85,6758.5,10195.2,10375.6,9858.86,5568.48,4405.4,3485.8,-3174.62,-2976.94,-2805.85,-470.296,873.375,-603.355,+7482 more]
  NodeStressYZ = [18.9286,-25.7554,443.465,349.377,457.003,1510.74,3505.53,1815.62,864.099,1508.87,747.01,78.0126,-61.3246,81.2199,-567.317,-1237.9,-959.419,-1702.45,-4595.42,-2141.46,-947.034,-1476.42,-443.423,53.3527,602.659,99.7814,308.228,138.848,+7483 more]
  NodeStressZZ = [95.9185,-299.981,303.32,945.571,139.58,1436.76,1744.36,2206.33,740.491,716.709,528.458,-281.983,-217.804,424.725,932.508,232.63,376.116,1752.45,1960.21,1580.57,136,554.321,672.732,-557.359,-432.308,198.237,51.6002,552.762,-316.433,-68.9846,+7481 more]
  PrincipalMax = [507.451,3034.07,4608.52,2990.47,6004.91,13887.4,14079.9,13267.9,6016.49,6274.88,5107.53,798.439,113.586,429.993,4384.55,7139.42,8479.84,15740.1,17998.3,12804.6,6191.46,5233.16,3793.4,-459.067,237.313,296.027,787.664,2712.7,2193.96,433.525,+7481 more]
  PrincipalMed = [388.659,-323.382,255.337,946.04,99.608,7222.81,7315.75,7487.39,3844.59,3288.9,2895.14,-246.692,-393.228,-726.088,810.273,-37.0449,235.019,8213,9707.52,9053.04,1689.48,1574.56,766.35,-3068.71,-2924.42,-2506.49,-435.711,922.343,-21.9003,+7482 more]
  PrincipalMin = [-2580.91,-714.095,-2054.9,-3138.76,-578.271,1126.52,161.024,1793.02,563.3,53.664,302.009,-2889.61,-3655.78,-5279.2,-3954.79,-2641.06,-1238.71,1385.05,-200.994,1006.38,-54.1608,-231.48,579.316,-4306,-4132.66,-4897.39,-681.758,159.23,+7483 more]
  ResultType = Fem::ResultMechanical
  Stats = [-11.4155,9.0655,-12.0586,9.70203,-109.804,52.5835,0,109.871,88.4364,88837.4,-29915.4,116644,-40391.3,41487,-123526,28332.9,49.3354,46805.4,0,0,0,0,0,0,0,0]
  Time = 0
  vonMises = [3030.71,3568.89,5860.4,5405.22,6271.78,11054.9,12055.7,9937.6,4755.06,5389.17,4166.06,3292.34,3543.25,5227.92,7246.58,8773.26,9071.91,12436.8,15781.8,10440.8,5581.93,4822.31,3124.77,3401.47,3908.52,4502.34,1363.16,2270.24,3116.71,1019.02,+7481 more]
FEATURE [Fem::FemPostPipeline] Pipeline_CCX_EigenMode_10_Results
  Mode = 2
FEATURE [App::TextDocument] ccx_dat_file
  Text = <blob: 5607 chars omitted>
FEATURE [Fem::FemAnalysis] Analysis
  Group = -> [MaterialSolid,FEMMeshGmsh,SolverCalculix,Pipeline_CalculiX_static_Results,ConstraintFixed,SolverCcxTools,SolverCalculix001,ResultPipeline,ConstraintForce,ConstraintForce001,ConstraintForce002,ConstraintForce003,Pipeline_CCX_Results,SolverCcxTools001,CCX_EigenMode_1_Results,Pipeline_CCX_EigenMode_1_Results,CCX_EigenMode_2_Results,Pipeline_CCX_EigenMode_2_Results,CCX_EigenMode_3_Results,+16 more]
